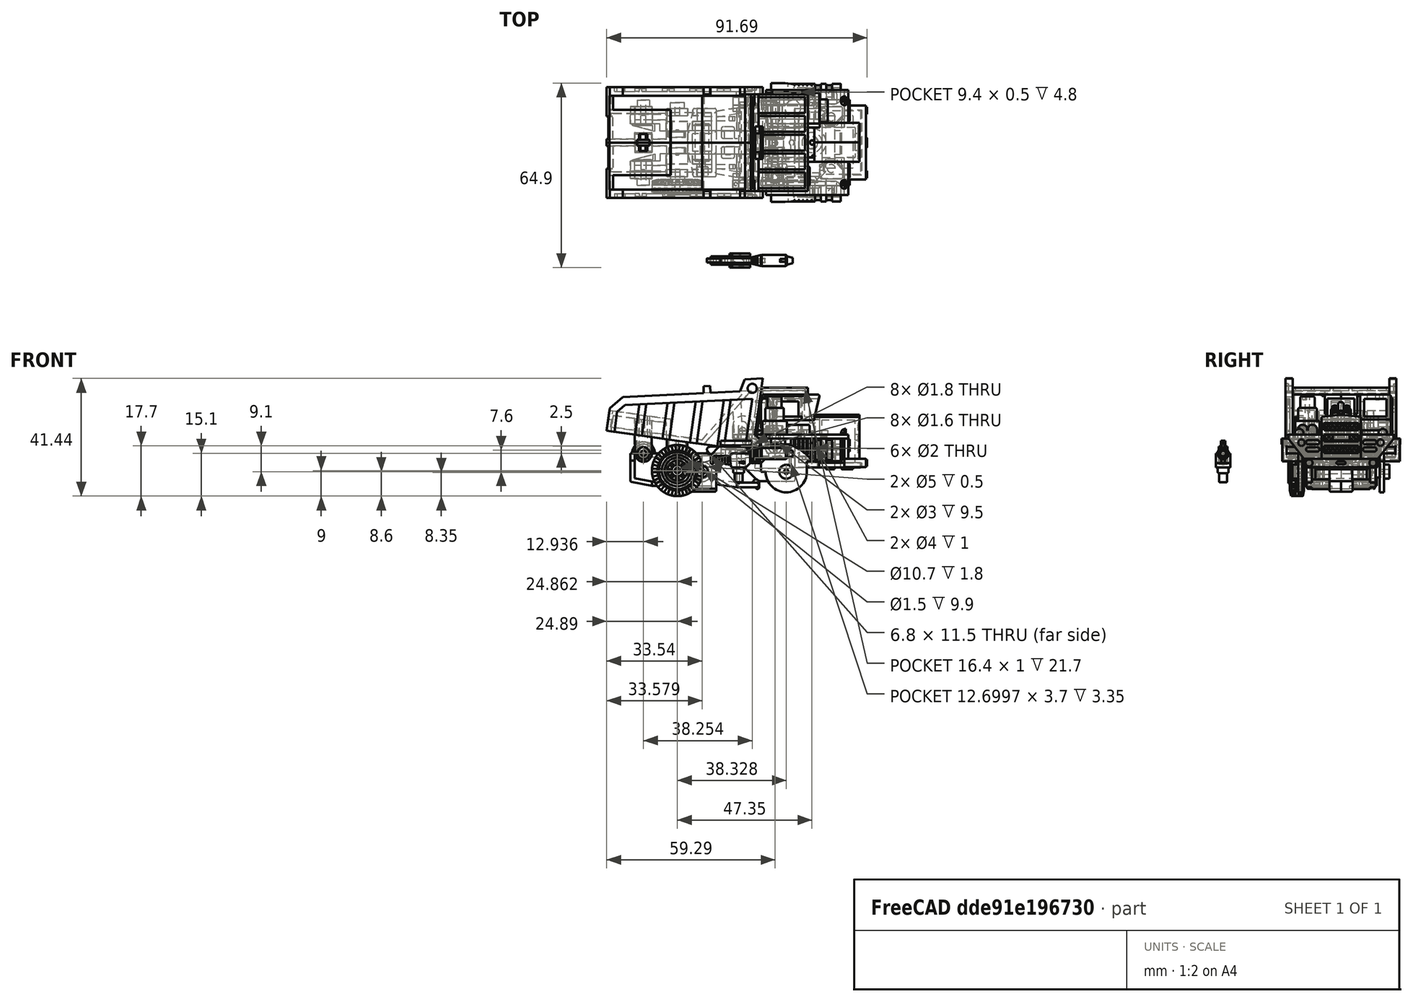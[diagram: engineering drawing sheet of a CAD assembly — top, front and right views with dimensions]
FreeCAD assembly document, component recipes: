
FREECAD ASSEMBLY — COMPONENT RECIPES ("Longhaul")

This assembly document has 21 components, labeled P0..P20 below (a component is one placed body or linked part). 19 of them carry a construction recipe — the FreeCAD feature program that regenerates the part from scratch, quoted from this document or its linked companion documents; the rest are supplied as boundary geometry only. No exploded tour is included for this assembly.
NOTE — document 2 of 4 of this assembly tour. The two overview renders and the header above are repeated from document 1; the component sections below continue where the previous document stopped.
COMPONENT P3 — recipe-attached ("Pre_Left_Leg", modeled in this document).
Construction recipe (the document's own serialized feature program — sketch geometry with constraints, then the solid features built on it; lengths are millimeters unless a unit is written):

FEATURE [PartDesign::SubShapeBinder] Binder002
  BindCopyOnChange = 0
  BindMode = 2
  ClaimChildren = false
  Context = -> Body003 [Binder002.]
  Fuse = false
  MakeFace = true
  OffsetFill = false
  OffsetIntersection = false
  OffsetJoinType = 0
  OffsetOpenResult = false
  PartialLoad = false
  Refine = true
  Relative = true
  _Version = 2
FEATURE [Sketcher::SketchObject] Sketch124
  ArcFitTolerance = 1e-06
  AttachmentSupport = -> [Binder002]
  ExternalGeometry = -> [Binder002]
  FullyConstrained = true
  MakeInternals = false
  MapMode = 5
  Placement = pos=(0,-7.1,0) rot=(1,0,0;1.5708rad)
  sketch-geometry (6):
    g0: ArcOfCircle CenterX=-23.6 CenterY=7.5 CenterZ=0 NormalX=0 NormalY=0 NormalZ=1 AngleXU=0 Radius=2.5 StartAngle=1.5708 EndAngle=4.71239
    g1: LineSegment StartX=-23.6 StartY=10 StartZ=0 EndX=-19.1 EndY=10 EndZ=0
    g2: LineSegment StartX=-19.1 StartY=10 StartZ=0 EndX=-19.1 EndY=2.1 EndZ=0
    g3: LineSegment StartX=-19.1 StartY=2.1 StartZ=0 EndX=-22.1 EndY=2.1 EndZ=0
    g4: LineSegment StartX=-22.1 StartY=2.1 StartZ=0 EndX=-22.1 EndY=5 EndZ=0
    g5: LineSegment StartX=-22.1 StartY=5 StartZ=0 EndX=-23.6 EndY=5 EndZ=0
  constraints (18):
    c: PointOnObject(g0,g-4)
    c: Coincident(g0,g-4)
    c: DistanceX(g0,g0) = 0
    c: DistanceX(g0,g0) = 0
    c: Coincident(g1,g0)
    c: Horizontal(g1)
    c: Coincident(g2,g1)
    c: Vertical(g2)
    c: Coincident(g3,g2)
    c: Horizontal(g3)
    c: Coincident(g4,g3)
    c: Vertical(g4)
    c: Coincident(g5,g4)
    c: Coincident(g5,g0)
    c: Horizontal(g5)
    c: DistanceX(g3,g3) = 3
    c: DistanceY(g2,g2) = 7.9
    c: DistanceX(g5,g5) = 1.5
FEATURE [PartDesign::Pad] Pad073
  Direction = (0,-1,2e-16)
  Length = 5.1
  Length2 = 10
  Profile = -> Sketch124
  ReferenceAxis = -> Sketch124 [N_Axis]
  Refine = true
  Suppressed = false
  Type = 0
FEATURE [Sketcher::SketchObject] Sketch125
  ArcFitTolerance = 1e-06
  AttachmentSupport = -> [Pad073]
  ExternalGeometry = -> [Pad073]
  FullyConstrained = true
  MakeInternals = false
  MapMode = 5
  Placement = pos=(0,-7.1,1.6e-15) rot=(0,0.707107,0.707107;3.14159rad)
  sketch-geometry (6):
    g0: LineSegment StartX=19.1 StartY=10 StartZ=0 EndX=19.1 EndY=2.1 EndZ=0
    g1: LineSegment StartX=19.1 StartY=2.1 StartZ=0 EndX=22.1 EndY=2.1 EndZ=0
    g2: LineSegment StartX=22.1 StartY=2.1 StartZ=0 EndX=22.1 EndY=5 EndZ=0
    g3: LineSegment StartX=22.1 StartY=5 StartZ=0 EndX=20.6 EndY=5 EndZ=0
    g4: LineSegment StartX=20.6 StartY=5 StartZ=0 EndX=20.6 EndY=10 EndZ=0
    g5: LineSegment StartX=20.6 StartY=10 StartZ=0 EndX=19.1 EndY=10 EndZ=0
  constraints (15):
    c: Coincident(g0,g-6)
    c: Coincident(g0,g-5)
    c: Coincident(g1,g0)
    c: Coincident(g1,g-4)
    c: PointOnObject(g2,g1)
    c: Coincident(g2,g-3)
    c: Vertical(g2)
    c: Coincident(g3,g2)
    c: Horizontal(g3)
    c: PointOnObject(g4,g-6)
    c: Coincident(g5,g4)
    c: Coincident(g5,g0)
    c: Coincident(g3,g4)
    c: DistanceX(g5,g5) = 1.5
    c: Vertical(g4)
FEATURE [PartDesign::Pad] Pad074
  BaseFeature = -> Pad073
  Direction = (0,1,-2e-16)
  Length = 3
  Length2 = 10
  Profile = -> Sketch125
  ReferenceAxis = -> Sketch125 [N_Axis]
  Refine = true
  Suppressed = false
  Type = 0
FEATURE [Sketcher::SketchObject] Sketch126
  ArcFitTolerance = 1e-06
  AttachmentSupport = -> [Pad074]
  ExternalGeometry = -> [Pad074]
  FullyConstrained = true
  MakeInternals = false
  MapMode = 5
  Placement = pos=(0,-12.2,2.8e-15) rot=(1,0,0;1.5708rad)
  sketch-geometry (1):
    g0: Circle CenterX=-23.6 CenterY=7.5 CenterZ=0 NormalX=0 NormalY=0 NormalZ=1 AngleXU=0 Radius=0.75
  constraints (2):
    c: Coincident(g0,g-3)
    c: Diameter(g0) = 1.5
FEATURE [PartDesign::Pocket] Pocket055
  BaseFeature = -> Pad074
  Direction = (0,1,-2e-16)
  Length = 6
  Length2 = 5
  Profile = -> Sketch126
  ReferenceAxis = -> Sketch126 [N_Axis]
  Refine = true
  Suppressed = false
  Type = 0
FEATURE [Sketcher::SketchObject] Sketch127
  ArcFitTolerance = 1e-06
  AttachmentSupport = -> [Pocket055]
  ExternalGeometry = -> [Pocket055]
  FullyConstrained = true
  MakeInternals = false
  MapMode = 5
  Placement = pos=(0,-12.2,2.8e-15) rot=(1,0,0;1.5708rad)
  sketch-geometry (8):
    g0: LineSegment StartX=-10.77 StartY=2.1 StartZ=0 EndX=-10.77 EndY=7.75 EndZ=0
    g1: ArcOfCircle CenterX=-10.77 CenterY=8.875 CenterZ=0 NormalX=0 NormalY=0 NormalZ=1 AngleXU=0 Radius=1.125 StartAngle=1.5708 EndAngle=4.71239
    g2: LineSegment StartX=-10.77 StartY=10 StartZ=0 EndX=-9.17 EndY=10 EndZ=0
    g3: ArcOfCircle CenterX=-9.17 CenterY=9.35 CenterZ=0 NormalX=0 NormalY=0 NormalZ=1 AngleXU=0 Radius=0.65 StartAngle=4.71239 EndAngle=7.85398
    g4: LineSegment StartX=-9.17 StartY=8.7 StartZ=0 EndX=-9.17 EndY=1.1 EndZ=0
    g5: LineSegment StartX=-9.17 StartY=1.1 StartZ=0 EndX=-21.1 EndY=1.1 EndZ=0
    g6: LineSegment StartX=-21.1 StartY=1.1 StartZ=0 EndX=-21.1 EndY=2.1 EndZ=0
    g7: LineSegment StartX=-21.1 StartY=2.1 StartZ=0 EndX=-10.77 EndY=2.1 EndZ=0
  constraints (27):
    c: Coincident(g1,g0)
    c: Coincident(g2,g1)
    c: Horizontal(g2)
    c: Coincident(g3,g2)
    c: Coincident(g4,g3)
    c: Vertical(g4)
    c: Coincident(g5,g4)
    c: Horizontal(g5)
    c: Coincident(g6,g5)
    c: DistanceY(g6,g6) = 1
    c: Vertical(g0)
    c: DistanceX(g-3,g0) = 8.33
    c: Diameter(g1) = 2.25
    c: DistanceX(g1,g0) = 0
    c: DistanceX(g1,g1) = 0
    c: DistanceX(g2,g2) = 1.6
    c: Diameter(g3) = 1.3
    c: DistanceX(g3,g2) = 0
    c: DistanceX(g3,g3) = 0
    c: DistanceY(g-4,g-4) = 7.9
    c: DistanceY(g0,g1) = 7.9
    c: Vertical(g6)
    c: DistanceX(g-3,g6) = 1
    c: Coincident(g7,g6)
    c: Coincident(g7,g0)
    c: Horizontal(g7)
    c: PointOnObject(g6,g-3)
FEATURE [PartDesign::Pad] Pad075
  BaseFeature = -> Pocket055
  Direction = (0,-1,2e-16)
  Length = 8.1
  Length2 = 10
  Profile = -> Sketch127
  ReferenceAxis = -> Sketch127 [N_Axis]
  Refine = true
  Reversed = true
  Suppressed = false
  Type = 0
FEATURE [Sketcher::SketchObject] Sketch128
  ArcFitTolerance = 1e-06
  AttachmentSupport = -> [Pad075]
  ExternalGeometry = -> [Pad075]
  FullyConstrained = true
  MakeInternals = false
  MapMode = 5
  Placement = pos=(0,5e-16,2.1) rot=(0,0,1;0rad)
  sketch-geometry (4):
    g0: LineSegment StartX=-19.1 StartY=-4.1 StartZ=0 EndX=-19.1 EndY=-10.2 EndZ=0
    g1: LineSegment StartX=-19.1 StartY=-10.2 StartZ=0 EndX=-10.77 EndY=-10.2 EndZ=0
    g2: LineSegment StartX=-10.77 StartY=-10.2 StartZ=0 EndX=-10.77 EndY=-4.1 EndZ=0
    g3: LineSegment StartX=-10.77 StartY=-4.1 StartZ=0 EndX=-19.1 EndY=-4.1 EndZ=0
  constraints (11):
    c: Coincident(g0,g1)
    c: Coincident(g1,g2)
    c: Coincident(g2,g3)
    c: Coincident(g3,g0)
    c: Vertical(g0)
    c: Vertical(g2)
    c: Horizontal(g1)
    c: Horizontal(g3)
    c: PointOnObject(g1,g-4)
    c: DistanceY(g-6,g1) = 2
    c: Coincident(g0,g-5)
FEATURE [PartDesign::Pocket] Pocket056
  BaseFeature = -> Pad075
  Direction = (0,0,-1)
  Length = 5
  Length2 = 5
  Profile = -> Sketch128
  ReferenceAxis = -> Sketch128 [N_Axis]
  Refine = true
  Suppressed = false
  Type = 0
FEATURE [Sketcher::SketchObject] Sketch129
  ArcFitTolerance = 1e-06
  AttachmentSupport = -> [Pocket056]
  ExternalGeometry = -> [Pocket056]
  FullyConstrained = true
  MakeInternals = false
  MapMode = 5
  Placement = pos=(0,-12.2,0) rot=(1,0,0;1.5708rad)
  sketch-geometry (4):
    g0: ArcOfCircle CenterX=-10.77 CenterY=8.875 CenterZ=0 NormalX=0 NormalY=0 NormalZ=1 AngleXU=0 Radius=1.125 StartAngle=1.5708 EndAngle=4.71239
    g1: ArcOfCircle CenterX=-9.17 CenterY=9.35 CenterZ=0 NormalX=0 NormalY=0 NormalZ=1 AngleXU=0 Radius=0.65 StartAngle=4.71239 EndAngle=7.85398
    g2: LineSegment StartX=-10.77 StartY=10 StartZ=0 EndX=-10.77 EndY=7.75 EndZ=0
    g3: LineSegment StartX=-9.17 StartY=10 StartZ=0 EndX=-9.17 EndY=8.7 EndZ=0
  constraints (8):
    c: Tangent(g0,g-4) = -1.5708
    c: Coincident(g0,g-4)
    c: Tangent(g1,g-3) = -1.5708
    c: Coincident(g1,g-3)
    c: Coincident(g2,g0)
    c: Coincident(g2,g0)
    c: Coincident(g3,g1)
    c: Coincident(g3,g1)
FEATURE [PartDesign::Pocket] Pocket057
  BaseFeature = -> Pocket056
  Direction = (0,1,-2e-16)
  Length = 2
  Length2 = 5
  Profile = -> Sketch129
  ReferenceAxis = -> Sketch129 [N_Axis]
  Refine = true
  Suppressed = false
  Type = 0
FEATURE [PartDesign::Fillet] Fillet004
  Base = -> Pocket057 [Edge38,Edge37]
  BaseFeature = -> Pocket057
  Radius = 0.5
  Refine = true
  SupportTransform = false
  Suppressed = false
  UseAllEdges = false
FEATURE [Sketcher::SketchObject] Sketch130
  ArcFitTolerance = 1e-06
  AttachmentSupport = -> [Fillet004]
  ExternalGeometry = -> [Fillet004]
  FullyConstrained = true
  MakeInternals = false
  MapMode = 5
  Placement = pos=(0,-12.2,0) rot=(1,0,0;1.5708rad)
  sketch-geometry (4):
    g0: LineSegment StartX=-10.77 StartY=2.1 StartZ=0 EndX=-10.77 EndY=3.1 EndZ=0
    g1: LineSegment StartX=-10.77 StartY=3.1 StartZ=0 EndX=-19.1 EndY=3.1 EndZ=0
    g2: LineSegment StartX=-19.1 StartY=3.1 StartZ=0 EndX=-19.1 EndY=2.1 EndZ=0
    g3: LineSegment StartX=-19.1 StartY=2.1 StartZ=0 EndX=-10.77 EndY=2.1 EndZ=0
  constraints (11):
    c: Coincident(g0,g1)
    c: Coincident(g1,g2)
    c: Coincident(g2,g3)
    c: Coincident(g3,g0)
    c: Vertical(g0)
    c: Vertical(g2)
    c: Horizontal(g1)
    c: Horizontal(g3)
    c: Coincident(g0,g-5)
    c: PointOnObject(g1,g-4)
    c: DistanceY(g2,g2) = 1
FEATURE [PartDesign::Pad] Pad076
  BaseFeature = -> Fillet004
  Direction = (0,-1,2e-16)
  Length = 2
  Length2 = 10
  Profile = -> Sketch130
  ReferenceAxis = -> Sketch130 [N_Axis]
  Refine = true
  Reversed = true
  Suppressed = false
  Type = 0
FEATURE [Sketcher::SketchObject] Sketch131
  ArcFitTolerance = 1e-06
  AttachmentSupport = -> [Pad076]
  ExternalGeometry = -> [Pad076]
  FullyConstrained = true
  MakeInternals = false
  MapMode = 5
  Placement = pos=(0,-12.2,0) rot=(1,0,0;1.5708rad)
  sketch-geometry (4):
    g0: LineSegment StartX=-21.1 StartY=2.1 StartZ=0 EndX=-21.1 EndY=1.1 EndZ=0
    g1: LineSegment StartX=-21.1 StartY=1.1 StartZ=0 EndX=-9.17 EndY=1.1 EndZ=0
    g2: LineSegment StartX=-9.17 StartY=1.1 StartZ=0 EndX=-9.17 EndY=2.1 EndZ=0
    g3: LineSegment StartX=-9.17 StartY=2.1 StartZ=0 EndX=-21.1 EndY=2.1 EndZ=0
  constraints (10):
    c: Coincident(g0,g1)
    c: Coincident(g1,g2)
    c: Coincident(g2,g3)
    c: Coincident(g3,g0)
    c: Vertical(g0)
    c: Vertical(g2)
    c: Horizontal(g1)
    c: Horizontal(g3)
    c: Coincident(g0,g-3)
    c: Coincident(g1,g-5)
FEATURE [PartDesign::Pocket] Pocket058
  BaseFeature = -> Pad076
  Direction = (0,1,-2e-16)
  Length = 9
  Length2 = 5
  Profile = -> Sketch131
  ReferenceAxis = -> Sketch131 [N_Axis]
  Refine = true
  Suppressed = false
  Type = 0
FEATURE [Sketcher::SketchObject] Sketch132
  ArcFitTolerance = 1e-06
  AttachmentOffset = pos=(0,0,-1) rot=(0,0,1;0rad)
  AttachmentSupport = -> [Pocket058]
  ExternalGeometry = -> [Pocket058]
  FullyConstrained = true
  MakeInternals = false
  MapMode = 5
  Placement = pos=(-21.1,0,0) rot=(0.57735,-0.57735,-0.57735;2.0944rad)
  sketch-geometry (16):
    g0: LineSegment StartX=12.2 StartY=2.1 StartZ=0 EndX=11 EndY=-5.15 EndZ=0
    g1: LineSegment StartX=4 StartY=-24.9 StartZ=0 EndX=6.5 EndY=-24.9 EndZ=0
    g2: LineSegment StartX=6.5 StartY=-24.9 StartZ=0 EndX=6.5 EndY=-35.4 EndZ=0
    g3: LineSegment StartX=6.5 StartY=-35.4 StartZ=0 EndX=10 EndY=-35.4 EndZ=0
    g4: LineSegment StartX=10 StartY=-35.4 StartZ=0 EndX=10 EndY=-22.8 EndZ=0
    g5: LineSegment StartX=10 StartY=-22.8 StartZ=0 EndX=9.5 EndY=-22.8 EndZ=0
    g6: LineSegment StartX=9.5 StartY=-22.8 StartZ=0 EndX=9.5 EndY=-11.9 EndZ=0
    g7: LineSegment StartX=9.5 StartY=-11.9 StartZ=0 EndX=12 EndY=-11.9 EndZ=0
    g8: LineSegment StartX=12 StartY=-11.9 StartZ=0 EndX=12 EndY=-5.15 EndZ=0
    g9: LineSegment StartX=12 StartY=-5.15 StartZ=0 EndX=11 EndY=-5.15 EndZ=0
    g10: LineSegment StartX=4.1 StartY=2.1 StartZ=0 EndX=4.1 EndY=-5.15 EndZ=0
    g11: LineSegment StartX=4.1 StartY=-5.15 StartZ=0 EndX=-1.8e-15 EndY=-5.15 EndZ=0
    g12: LineSegment StartX=-1.8e-15 StartY=-5.15 StartZ=0 EndX=-1.8e-15 EndY=-15.15 EndZ=0
    g13: LineSegment StartX=4 StartY=-24.9 StartZ=0 EndX=4 EndY=-15.15 EndZ=0
    g14: LineSegment StartX=4 StartY=-15.15 StartZ=0 EndX=-1.8e-15 EndY=-15.15 EndZ=0
    g15: LineSegment StartX=4.1 StartY=2.1 StartZ=0 EndX=12.2 EndY=2.1 EndZ=0
  constraints (47):
    c: Coincident(g0,g-3)
    c: Horizontal(g1)
    c: Coincident(g2,g1)
    c: Vertical(g2)
    c: Coincident(g3,g2)
    c: Horizontal(g3)
    c: Coincident(g4,g3)
    c: Vertical(g4)
    c: Coincident(g5,g4)
    c: Horizontal(g5)
    c: Coincident(g6,g5)
    c: Vertical(g6)
    c: Coincident(g7,g6)
    c: Horizontal(g7)
    c: Coincident(g8,g7)
    c: Vertical(g8)
    c: Coincident(g9,g8)
    c: Coincident(g9,g0)
    c: Horizontal(g9)
    c: DistanceX(g1,g6) = 5.5
    c: DistanceY(g8,g8) = 6.75
    c: DistanceY(g8,g0) = 7.25
    c: DistanceX(g9,g9) = 1
    c: Coincident(g10,g-3)
    c: Vertical(g10)
    c: Coincident(g11,g10)
    c: Horizontal(g11)
    c: Coincident(g12,g11)
    c: Vertical(g12)
    c: Coincident(g13,g1)
    c: Vertical(g13)
    c: Coincident(g14,g13)
    c: Coincident(g14,g12)
    c: Horizontal(g14)
    c: DistanceX(g11,g8) = 12
    c: DistanceX(g7,g7) = 2.5
    c: DistanceY(g10,g10) = 7.25
    c: DistanceY(g12,g12) = 10
    c: DistanceX(g11,g11) = 4.1
    c: DistanceX(g1,g1) = 2.5
    c: DistanceY(g3,g-4) = 45.4
    c: DistanceY(g1,g-5) = 34.9
    c: DistanceX(g5,g5) = 0.5
    c: DistanceX(g3,g3) = 3.5
    c: DistanceY(g4,g4) = 12.6
    c: Coincident(g15,g10)
    c: Coincident(g15,g0)
FEATURE [PartDesign::Pad] Pad077
  BaseFeature = -> Pocket058
  Direction = (-1,0,0)
  Length = 1
  Length2 = 10
  Profile = -> Sketch132
  ReferenceAxis = -> Sketch132 [N_Axis]
  Refine = true
  Reversed = true
  Suppressed = false
  Type = 0
FEATURE [Sketcher::SketchObject] Sketch133
  ArcFitTolerance = 1e-06
  AttachmentSupport = -> [Pad077]
  ExternalGeometry = -> [Pad077]
  FullyConstrained = true
  MakeInternals = false
  MapMode = 5
  Placement = pos=(-20.1,0,0) rot=(0.57735,0.57735,0.57735;2.0944rad)
  sketch-geometry (4):
    g0: LineSegment StartX=-4.1 StartY=2.1 StartZ=0 EndX=-12.2 EndY=2.1 EndZ=0
    g1: LineSegment StartX=-12.2 StartY=2.1 StartZ=0 EndX=-11 EndY=-5.15 EndZ=0
    g2: LineSegment StartX=-11 StartY=-5.15 StartZ=0 EndX=-4.1 EndY=-5.15 EndZ=0
    g3: LineSegment StartX=-4.1 StartY=-5.15 StartZ=0 EndX=-4.1 EndY=2.1 EndZ=0
  constraints (8):
    c: Coincident(g0,g-3)
    c: Coincident(g0,g-4)
    c: Coincident(g1,g0)
    c: Coincident(g1,g-4)
    c: Coincident(g2,g1)
    c: Coincident(g2,g-3)
    c: Coincident(g3,g2)
    c: Coincident(g3,g0)
FEATURE [PartDesign::Pad] Pad078
  BaseFeature = -> Pad077
  Direction = (1,0,0)
  Length = 1
  Length2 = 10
  Profile = -> Sketch133
  ReferenceAxis = -> Sketch133 [N_Axis]
  Refine = true
  Suppressed = false
  Type = 0
FEATURE [Sketcher::SketchObject] Sketch134
  ArcFitTolerance = 1e-06
  AttachmentSupport = -> [Pad078]
  ExternalGeometry = -> [Pad078]
  FullyConstrained = true
  MakeInternals = false
  MapMode = 5
  Placement = pos=(-20.1,0,0) rot=(0.57735,0.57735,0.57735;2.0944rad)
  sketch-geometry (8):
    g0: LineSegment StartX=-4 StartY=-15.15 StartZ=0 EndX=-4 EndY=-24.9 EndZ=0
    g1: LineSegment StartX=-4 StartY=-24.9 StartZ=0 EndX=-6.5 EndY=-24.9 EndZ=0
    g2: LineSegment StartX=-6.5 StartY=-24.9 StartZ=0 EndX=-6.5 EndY=-35.4 EndZ=0
    g3: LineSegment StartX=-6.5 StartY=-35.4 StartZ=0 EndX=-10 EndY=-35.4 EndZ=0
    g4: LineSegment StartX=-10 StartY=-35.4 StartZ=0 EndX=-10 EndY=-22.8 EndZ=0
    g5: LineSegment StartX=-4 StartY=-15.15 StartZ=0 EndX=-9.5 EndY=-15.15 EndZ=0
    g6: LineSegment StartX=-9.5 StartY=-15.15 StartZ=0 EndX=-9.5 EndY=-22.8 EndZ=0
    g7: LineSegment StartX=-9.5 StartY=-22.8 StartZ=0 EndX=-10 EndY=-22.8 EndZ=0
  constraints (17):
    c: Coincident(g0,g-3)
    c: Coincident(g0,g-9)
    c: Coincident(g1,g0)
    c: Coincident(g1,g-9)
    c: Coincident(g2,g1)
    c: Coincident(g2,g-6)
    c: Coincident(g3,g2)
    c: Coincident(g3,g-7)
    c: Coincident(g4,g3)
    c: Coincident(g4,g-8)
    c: Coincident(g5,g0)
    c: PointOnObject(g5,g-4)
    c: Horizontal(g5)
    c: Coincident(g6,g5)
    c: Coincident(g6,g-8)
    c: Coincident(g7,g4)
    c: Coincident(g6,g7)
FEATURE [PartDesign::Pad] Pad079
  BaseFeature = -> Pad078
  Direction = (1,0,0)
  Length = 0.5
  Length2 = 10
  Profile = -> Sketch134
  ReferenceAxis = -> Sketch134 [N_Axis]
  Refine = true
  Suppressed = false
  Type = 0
FEATURE [Sketcher::SketchObject] Sketch135
  ArcFitTolerance = 1e-06
  AttachmentSupport = -> [Pad079]
  ExternalGeometry = -> [Pad079]
  FullyConstrained = true
  MakeInternals = false
  MapMode = 5
  Placement = pos=(0,1.8e-15,0) rot=(0,0.707107,0.707107;3.14159rad)
  sketch-geometry (8):
    g0: LineSegment StartX=20.1 StartY=-5.15 StartZ=0 EndX=7.6 EndY=-5.15 EndZ=0
    g1: LineSegment StartX=20.1 StartY=-15.15 StartZ=0 EndX=7.6 EndY=-15.15 EndZ=0
    g2: LineSegment StartX=7.6 StartY=-5.15 StartZ=0 EndX=7.6 EndY=-15.15 EndZ=0
    g3: LineSegment StartX=20.1 StartY=-15.15 StartZ=0 EndX=20.1 EndY=-13.55 EndZ=0
    g4: LineSegment StartX=20.1 StartY=-13.55 StartZ=0 EndX=8.6 EndY=-13.55 EndZ=0
    g5: LineSegment StartX=8.6 StartY=-13.55 StartZ=0 EndX=8.6 EndY=-6.75 EndZ=0
    g6: LineSegment StartX=8.6 StartY=-6.75 StartZ=0 EndX=20.1 EndY=-6.75 EndZ=0
    g7: LineSegment StartX=20.1 StartY=-6.75 StartZ=0 EndX=20.1 EndY=-5.15 EndZ=0
  constraints (23):
    c: Coincident(g0,g-5)
    c: Horizontal(g0)
    c: Coincident(g1,g-4)
    c: Horizontal(g1)
    c: Coincident(g2,g0)
    c: Coincident(g2,g1)
    c: Vertical(g2)
    c: DistanceY(g-6,g-6) = 10
    c: Coincident(g3,g1)
    c: Vertical(g3)
    c: Coincident(g4,g3)
    c: Horizontal(g4)
    c: Coincident(g5,g4)
    c: Vertical(g5)
    c: Coincident(g6,g5)
    c: Horizontal(g6)
    c: PointOnObject(g6,g-7)
    c: Coincident(g7,g6)
    c: Coincident(g7,g0)
    c: DistanceX(g0,g5) = 1
    c: DistanceY(g5,g0) = 1.6
    c: DistanceY(g1,g4) = 1.6
    c: DistanceX(g0,g6) = 12.5
FEATURE [PartDesign::Pad] Pad080
  BaseFeature = -> Pad079
  Direction = (0,1,-2e-16)
  Length = 4.1
  Length2 = 10
  Profile = -> Sketch135
  ReferenceAxis = -> Sketch135 [N_Axis]
  Refine = true
  Reversed = true
  Suppressed = false
  Type = 0
FEATURE [Sketcher::SketchObject] Sketch136
  ArcFitTolerance = 1e-06
  AttachmentSupport = -> [Pad080]
  ExternalGeometry = -> [Pad080]
  FullyConstrained = true
  MakeInternals = false
  MapMode = 5
  Placement = pos=(0,-12,0) rot=(1,0,0;1.5708rad)
  sketch-geometry (6):
    g0: LineSegment StartX=-20.1 StartY=-5.15 StartZ=0 EndX=-8.6 EndY=-5.15 EndZ=0
    g1: LineSegment StartX=-8.6 StartY=-5.15 StartZ=0 EndX=-8.6 EndY=-13.35 EndZ=0
    g2: LineSegment StartX=-20.1 StartY=-11.9 StartZ=0 EndX=-17.3 EndY=-11.9 EndZ=0
    g3: LineSegment StartX=-8.6 StartY=-13.35 StartZ=0 EndX=-14.6 EndY=-13.35 EndZ=0
    g4: ArcOfCircle CenterX=-14.6 CenterY=-10.1112 CenterZ=0 NormalX=0 NormalY=0 NormalZ=1 AngleXU=0 Radius=3.23879 StartAngle=3.72672 EndAngle=4.71239
    g5: LineSegment StartX=-20.1 StartY=-5.15 StartZ=0 EndX=-20.1 EndY=-11.9 EndZ=0
  constraints (20):
    c: DistanceX(g-4,g-4) = 1
    c: Coincident(g0,g-4)
    c: Horizontal(g0)
    c: DistanceX(g0,g0) = 11.5
    c: Coincident(g1,g0)
    c: Vertical(g1)
    c: DistanceY(g1,g1) = 8.2
    c: Coincident(g2,g-3)
    c: Horizontal(g2)
    c: Coincident(g3,g1)
    c: Horizontal(g3)
    c: Coincident(g4,g3)
    c: Coincident(g4,g2)
    c: DistanceX(g2,g2) = 2.8
    c: DistanceX(g4,g3) = 0
    c: DistanceX(g-5,g4) = 6.5
    c: DistanceX(g3,g1) = 6
    c: DistanceX(g2,g1) = 8.7
    c: Coincident(g5,g2)
    c: Coincident(g5,g0)
FEATURE [PartDesign::Pad] Pad081
  BaseFeature = -> Pad080
  Direction = (0,-1,2e-16)
  Length = 1.5
  Length2 = 10
  Profile = -> Sketch136
  ReferenceAxis = -> Sketch136 [N_Axis]
  Refine = true
  Reversed = true
  Suppressed = false
  Type = 0
FEATURE [Sketcher::SketchObject] Sketch137
  ArcFitTolerance = 1e-06
  AttachmentSupport = -> [Pad081]
  ExternalGeometry = -> [Pad081]
  FullyConstrained = true
  MakeInternals = false
  MapMode = 5
  Placement = pos=(-19.1,0,4.6e-15) rot=(0.57735,0.57735,0.57735;2.0944rad)
  sketch-geometry (4):
    g0: LineSegment StartX=-12.2 StartY=2.1 StartZ=0 EndX=-10.2 EndY=2.1 EndZ=0
    g1: LineSegment StartX=-12.2 StartY=2.1 StartZ=0 EndX=-11 EndY=-5.15 EndZ=0
    g2: LineSegment StartX=-11 StartY=-5.15 StartZ=0 EndX=-9 EndY=-5.15 EndZ=0
    g3: LineSegment StartX=-9 StartY=-5.15 StartZ=0 EndX=-10.2 EndY=2.1 EndZ=0
  constraints (10):
    c: DistanceX(g-4,g-4) = 2
    c: Coincident(g0,g-4)
    c: Coincident(g0,g-4)
    c: Coincident(g1,g0)
    c: Coincident(g1,g-5)
    c: Coincident(g2,g1)
    c: PointOnObject(g2,g-6)
    c: Coincident(g3,g2)
    c: Coincident(g3,g0)
    c: DistanceX(g2,g2) = 2
FEATURE [PartDesign::Pad] Pad082
  BaseFeature = -> Pad081
  Direction = (1,0,0)
  Length = 9.93
  Length2 = 10
  Profile = -> Sketch137
  ReferenceAxis = -> Sketch137 [N_Axis]
  Refine = true
  Suppressed = false
  Type = 0
FEATURE [Sketcher::SketchObject] Sketch138
  ArcFitTolerance = 1e-06
  AttachmentSupport = -> [Pad082]
  ExternalGeometry = -> [Pad082]
  FullyConstrained = true
  MakeInternals = false
  MapMode = 5
  Placement = pos=(0,-12.2,0) rot=(1,0,0;1.5708rad)
  sketch-geometry (3):
    g0: LineSegment StartX=-9.17 StartY=2.1 StartZ=0 EndX=-9.17 EndY=-5.15 EndZ=0
    g1: LineSegment StartX=-9.17 StartY=-5.15 StartZ=0 EndX=-10.1 EndY=-5.15 EndZ=0
    g2: LineSegment StartX=-10.1 StartY=-5.15 StartZ=0 EndX=-9.17 EndY=2.1 EndZ=0
  constraints (7):
    c: Coincident(g0,g-3)
    c: Coincident(g0,g-3)
    c: Coincident(g1,g0)
    c: PointOnObject(g1,g-4)
    c: Coincident(g2,g1)
    c: Coincident(g2,g0)
    c: DistanceX(g-4,g1) = 11
FEATURE [PartDesign::Pocket] Pocket059
  BaseFeature = -> Pad082
  Direction = (0,1,-2e-16)
  Length = 5
  Length2 = 5
  Profile = -> Sketch138
  ReferenceAxis = -> Sketch138 [N_Axis]
  Refine = true
  Suppressed = false
  Type = 0
FEATURE [Sketcher::SketchObject] Sketch139
  ArcFitTolerance = 1e-06
  AttachmentSupport = -> [Pocket059]
  ExternalGeometry = -> [Pocket059]
  FullyConstrained = true
  MakeInternals = false
  MapMode = 5
  Placement = pos=(0,-4.1,0) rot=(0,0.707107,0.707107;3.14159rad)
  sketch-geometry (4):
    g0: LineSegment StartX=9.17 StartY=2.1 StartZ=0 EndX=10.77 EndY=2.1 EndZ=0
    g1: LineSegment StartX=9.17 StartY=2.1 StartZ=0 EndX=10.1 EndY=-5.15 EndZ=0
    g2: LineSegment StartX=10.1 StartY=-5.15 StartZ=0 EndX=11.7 EndY=-5.15 EndZ=0
    g3: LineSegment StartX=11.7 StartY=-5.15 StartZ=0 EndX=10.77 EndY=2.1 EndZ=0
  constraints (9):
    c: Coincident(g0,g-4)
    c: Coincident(g0,g-3)
    c: Coincident(g1,g0)
    c: Coincident(g1,g-4)
    c: Coincident(g2,g1)
    c: PointOnObject(g2,g-5)
    c: Coincident(g3,g2)
    c: Coincident(g3,g0)
    c: DistanceX(g2,g2) = 1.6
FEATURE [PartDesign::Pad] Pad083
  BaseFeature = -> Pocket059
  Direction = (0,1,-2e-16)
  Length = 6.5
  Length2 = 10
  Profile = -> Sketch139
  ReferenceAxis = -> Sketch139 [N_Axis]
  Refine = true
  Reversed = true
  Suppressed = false
  Type = 0
FEATURE [Sketcher::SketchObject] Sketch140
  ArcFitTolerance = 1e-06
  AttachmentSupport = -> [Pad083]
  ExternalGeometry = -> [Pad083]
  FullyConstrained = true
  MakeInternals = false
  MapMode = 5
  Placement = pos=(-8.6,0,0) rot=(0.57735,0.57735,0.57735;2.0944rad)
  sketch-geometry (4):
    g0: LineSegment StartX=-10.5 StartY=-5.15 StartZ=0 EndX=-4.1 EndY=-5.15 EndZ=0
    g1: LineSegment StartX=-4.1 StartY=-5.15 StartZ=0 EndX=-4.1 EndY=-15.15 EndZ=0
    g2: LineSegment StartX=-4.1 StartY=-15.15 StartZ=0 EndX=-10.5 EndY=-13.35 EndZ=0
    g3: LineSegment StartX=-10.5 StartY=-13.35 StartZ=0 EndX=-10.5 EndY=-5.15 EndZ=0
  constraints (8):
    c: Coincident(g0,g-3)
    c: Coincident(g0,g-4)
    c: Coincident(g1,g0)
    c: Coincident(g1,g-4)
    c: Coincident(g2,g1)
    c: Coincident(g2,g-3)
    c: Coincident(g3,g2)
    c: Coincident(g3,g0)
FEATURE [PartDesign::Pad] Pad084
  BaseFeature = -> Pad083
  Direction = (1,0,0)
  Length = 1
  Length2 = 10
  Profile = -> Sketch140
  ReferenceAxis = -> Sketch140 [N_Axis]
  Refine = true
  Reversed = true
  Suppressed = false
  Type = 0
FEATURE [Sketcher::SketchObject] Sketch141
  ArcFitTolerance = 1e-06
  AttachmentSupport = -> [Pad084]
  ExternalGeometry = -> [Pad084]
  FullyConstrained = false
  MakeInternals = false
  MapMode = 5
  Placement = pos=(0,-4.1,0) rot=(0,0.707107,0.707107;3.14159rad)
  sketch-geometry (4):
    g0: LineSegment StartX=8.6 StartY=-6.7914 StartZ=0 EndX=8.6 EndY=-13.55 EndZ=0
    g1: LineSegment StartX=8.6 StartY=-13.55 StartZ=0 EndX=9.6 EndY=-13.55 EndZ=0
    g2: LineSegment StartX=9.6 StartY=-13.55 StartZ=0 EndX=9.6 EndY=-6.7914 EndZ=0
    g3: LineSegment StartX=9.6 StartY=-6.7914 StartZ=0 EndX=8.6 EndY=-6.7914 EndZ=0
  constraints (10):
    c: Coincident(g0,g1)
    c: Coincident(g1,g2)
    c: Coincident(g2,g3)
    c: Coincident(g3,g0)
    c: Vertical(g0)
    c: Vertical(g2)
    c: Horizontal(g1)
    c: Horizontal(g3)
    c: PointOnObject(g0,g-3)
    c: Coincident(g1,g-4)
FEATURE [PartDesign::Pad] Pad085
  BaseFeature = -> Pad084
  Direction = (0,1,-2e-16)
  Length = 1
  Length2 = 10
  Profile = -> Sketch141
  ReferenceAxis = -> Sketch141 [N_Axis]
  Refine = true
  Suppressed = false
  Type = 0
FEATURE [Sketcher::SketchObject] Sketch142
  ArcFitTolerance = 1e-06
  AttachmentSupport = -> [Pad085]
  ExternalGeometry = -> [Pad085]
  FullyConstrained = true
  MakeInternals = false
  MapMode = 5
  Placement = pos=(0,-4.1,0) rot=(1,0,0;1.5708rad)
  sketch-geometry (4):
    g0: LineSegment StartX=-9.6 StartY=-5.15 StartZ=0 EndX=-20.1 EndY=-5.15 EndZ=0
    g1: LineSegment StartX=-20.1 StartY=-5.15 StartZ=0 EndX=-20.1 EndY=-6.75 EndZ=0
    g2: LineSegment StartX=-20.1 StartY=-6.75 StartZ=0 EndX=-9.6 EndY=-6.75 EndZ=0
    g3: LineSegment StartX=-9.6 StartY=-6.75 StartZ=0 EndX=-9.6 EndY=-5.15 EndZ=0
  constraints (10):
    c: Coincident(g0,g1)
    c: Coincident(g1,g2)
    c: Coincident(g2,g3)
    c: Coincident(g3,g0)
    c: Horizontal(g0)
    c: Horizontal(g2)
    c: Vertical(g1)
    c: Vertical(g3)
    c: Coincident(g0,g-6)
    c: Coincident(g1,g-5)
FEATURE [PartDesign::Pad] Pad086
  BaseFeature = -> Pad085
  Direction = (0,-1,2e-16)
  Length = 7
  Length2 = 10
  Profile = -> Sketch142
  ReferenceAxis = -> Sketch142 [N_Axis]
  Refine = true
  Suppressed = false
  Type = 0
FEATURE [Sketcher::SketchObject] Sketch143
  ArcFitTolerance = 1e-06
  AttachmentSupport = -> [Pad086]
  ExternalGeometry = -> [Pad086]
  FullyConstrained = true
  MakeInternals = false
  MapMode = 5
  Placement = pos=(0,-10.5,0) rot=(0,0.707107,0.707107;3.14159rad)
  sketch-geometry (8):
    g0: LineSegment StartX=9.6 StartY=-13.35 StartZ=0 EndX=14.6 EndY=-13.35 EndZ=0
    g1: ArcOfCircle CenterX=14.6 CenterY=-10.1112 CenterZ=0 NormalX=0 NormalY=0 NormalZ=1 AngleXU=0 Radius=3.23879 StartAngle=4.71239 EndAngle=5.69806
    g2: LineSegment StartX=17.3 StartY=-11.9 StartZ=0 EndX=20.1 EndY=-11.9 EndZ=0
    g3: LineSegment StartX=20.1 StartY=-11.9 StartZ=0 EndX=20.1 EndY=-10.4 EndZ=0
    g4: LineSegment StartX=20.1 StartY=-10.4 StartZ=0 EndX=16.3146 EndY=-10.4 EndZ=0
    g5: LineSegment StartX=9.6 StartY=-13.35 StartZ=0 EndX=9.6 EndY=-11.85 EndZ=0
    g6: LineSegment StartX=9.6 StartY=-11.85 StartZ=0 EndX=14.6 EndY=-11.85 EndZ=0
    g7: ArcOfCircle CenterX=14.6 CenterY=-10.1112 CenterZ=0 NormalX=0 NormalY=0 NormalZ=1 AngleXU=0 Radius=1.73879 StartAngle=4.71239 EndAngle=6.11632
  constraints (22):
    c: Coincident(g0,g-7)
    c: Coincident(g1,g0)
    c: Tangent(g1,g-5) = -1.5708
    c: PointOnObject(g2,g-5)
    c: Coincident(g2,g-4)
    c: Horizontal(g2)
    c: PointOnObject(g3,g2)
    c: PointOnObject(g3,g-3)
    c: Vertical(g3)
    c: Coincident(g4,g3)
    c: Horizontal(g4)
    c: Coincident(g0,g-6)
    c: Coincident(g5,g0)
    c: PointOnObject(g5,g-7)
    c: Coincident(g6,g5)
    c: Horizontal(g6)
    c: Coincident(g7,g6)
    c: Coincident(g7,g4)
    c: Coincident(g7,g1)
    c: DistanceY(g3,g3) = 1.5
    c: DistanceY(g5,g5) = 1.5
    c: DistanceX(g6,g0) = 0
FEATURE [PartDesign::Pad] Pad087
  BaseFeature = -> Pad086
  Direction = (0,1,-2e-16)
  Length = 1
  Length2 = 10
  Profile = -> Sketch143
  ReferenceAxis = -> Sketch143 [N_Axis]
  Refine = true
  Suppressed = false
  Type = 0
FEATURE [Sketcher::SketchObject] Sketch144
  ArcFitTolerance = 1e-06
  AttachmentSupport = -> [Pad087]
  ExternalGeometry = -> [Pad087]
  FullyConstrained = true
  MakeInternals = false
  MapMode = 5
  Placement = pos=(-9.9e-15,-9.5,0) rot=(1,0,0;1.5708rad)
  sketch-geometry (8):
    g0: LineSegment StartX=-19.6 StartY=-22.8 StartZ=0 EndX=-19.6 EndY=-15.15 EndZ=0
    g1: LineSegment StartX=-19.6 StartY=-15.15 StartZ=0 EndX=-20.1 EndY=-15.15 EndZ=0
    g2: LineSegment StartX=-20.1 StartY=-15.15 StartZ=0 EndX=-20.1 EndY=-10.4 EndZ=0
    g3: LineSegment StartX=-20.1 StartY=-10.4 StartZ=0 EndX=-16.3146 EndY=-10.4 EndZ=0
    g4: ArcOfCircle CenterX=-14.6 CenterY=-10.1112 CenterZ=0 NormalX=0 NormalY=0 NormalZ=1 AngleXU=0 Radius=1.73879 StartAngle=3.30845 EndAngle=4.71239
    g5: LineSegment StartX=-14.6 StartY=-11.85 StartZ=0 EndX=-9.6 EndY=-11.85 EndZ=0
    g6: LineSegment StartX=-19.6 StartY=-22.8 StartZ=0 EndX=-9.6 EndY=-22.8 EndZ=0
    g7: LineSegment StartX=-9.6 StartY=-11.85 StartZ=0 EndX=-9.6 EndY=-22.8 EndZ=0
  constraints (17):
    c: Coincident(g0,g-4)
    c: Coincident(g0,g-4)
    c: Coincident(g1,g0)
    c: Coincident(g1,g-3)
    c: Coincident(g2,g1)
    c: Coincident(g2,g-5)
    c: Coincident(g3,g2)
    c: Coincident(g3,g-7)
    c: Tangent(g4,g-7) = -1.5708
    c: Coincident(g4,g-8)
    c: Coincident(g5,g4)
    c: Coincident(g5,g-8)
    c: Coincident(g6,g0)
    c: Horizontal(g6)
    c: Coincident(g7,g5)
    c: Coincident(g6,g7)
    c: Vertical(g7)
FEATURE [PartDesign::Pad] Pad088
  BaseFeature = -> Pad087
  Direction = (-1e-15,-1,2e-16)
  Length = 2
  Length2 = 10
  Profile = -> Sketch144
  ReferenceAxis = -> Sketch144 [N_Axis]
  Refine = true
  Reversed = true
  Suppressed = false
  Type = 0
FEATURE [PartDesign::Body] Body003  label="Pre_Left_Leg"
  AllowCompound = false
  Group = -> [Binder002,Sketch124,Pad073,Sketch125,Pad074,Sketch126,Pocket055,Sketch127,Pad075,Sketch128,Pocket056,Sketch129,Pocket057,Fillet004,Sketch130,Pad076,Sketch131,Pocket058,Sketch132,Pad077,Sketch133,Pad078,Sketch134,Pad079,Sketch135,Pad080,Sketch136,Pad081,Sketch137,Pad082,Sketch138,Pocket059,Sketch139,Pad083,Sketch140,Pad084,Sketch141,Pad085,Sketch142,Pad086,Sketch143,Pad087,Sketch144,Pad088,+61 more]
  Origin = -> Origin003
  Placement = pos=(0,38,0) rot=(0,0,1;0rad)
  Tip = -> Pocket183
COMPONENT P4 — recipe-attached ("Right_Foot", modeled in this document).
Construction recipe (the document's own serialized feature program — sketch geometry with constraints, then the solid features built on it; lengths are millimeters unless a unit is written):

FEATURE [Sketcher::SketchObject] Sketch172
  ArcFitTolerance = 1e-06
  AttachmentSupport = -> [XY_Plane004]
  FullyConstrained = true
  MakeInternals = false
  MapMode = 5
  sketch-geometry (14):
    g0: LineSegment StartX=0 StartY=0 StartZ=0 EndX=43 EndY=0 EndZ=0
    g1: ArcOfCircle CenterX=50.8475 CenterY=2.65774 CenterZ=0 NormalX=0 NormalY=0 NormalZ=1 AngleXU=0 Radius=3.3 StartAngle=6.11336 EndAngle=7.54355
    g2: LineSegment StartX=51.8555 StartY=5.8 StartZ=0 EndX=51.8555 EndY=25.9 EndZ=0
    g3: LineSegment StartX=51.8555 StartY=25.9 StartZ=0 EndX=45.5709 EndY=24.6903 EndZ=0
    g4: LineSegment StartX=45.5709 StartY=24.6903 StartZ=0 EndX=44.5555 EndY=20.3063 EndZ=0
    g5: LineSegment StartX=44.5555 StartY=20.3063 StartZ=0 EndX=34.343 EndY=18.3406 EndZ=0
    g6: LineSegment StartX=34.343 StartY=18.3406 StartZ=0 EndX=33.8894 EndY=20.6973 EndZ=0
    g7: LineSegment StartX=33.8894 StartY=20.6973 StartZ=0 EndX=31.5326 EndY=20.2437 EndZ=0
    g8: LineSegment StartX=31.5326 StartY=20.2437 StartZ=0 EndX=31.9863 EndY=17.8869 EndZ=0
    g9: LineSegment StartX=31.9863 StartY=17.8869 StartZ=0 EndX=4 EndY=12.5 EndZ=0
    g10: LineSegment StartX=4 StartY=12.5 StartZ=0 EndX=0 EndY=8 EndZ=0
    g11: LineSegment StartX=0 StartY=8 StartZ=0 EndX=0 EndY=0 EndZ=0
    g12: ArcOfCircle CenterX=43 CenterY=15.82 CenterZ=0 NormalX=0 NormalY=0 NormalZ=1 AngleXU=0 Radius=15.82 StartAngle=4.71239 EndAngle=4.90962
    g13: LineSegment StartX=46.1 StartY=0.306702 StartZ=0 EndX=54.1 EndY=2.1 EndZ=0
  constraints (44):
    c: Coincident(g0,g-1)
    c: Coincident(g2,g1)
    c: Vertical(g2)
    c: Coincident(g3,g2)
    c: Coincident(g4,g3)
    c: Coincident(g5,g4)
    c: Coincident(g6,g5)
    c: Coincident(g7,g6)
    c: Coincident(g8,g7)
    c: Coincident(g10,g9)
    c: PointOnObject(g10,g-2)
    c: Coincident(g11,g10)
    c: Coincident(g11,g0)
    c: Parallel(g7,g5)
    c: Parallel(g3,g5)
    c: Parallel(g7,g9)
    c: Distance(g7) = 2.4
    c: Distance(g5) = 10.4
    c: Angle(g5,g6) = 1.5708
    c: Angle(g8,g9) = 1.5708
    c: Distance(g3) = 6.4
    c: DistanceY(g11,g11) = 8
    c: Distance(g8) = 2.4
    c: Distance(g6) = 2.4
    c: Coincident(g9,g8)
    c: Distance(g4) = 4.5
    c: DistanceX(g4,g2) = 7.3
    c: DistanceX(g0,g9) = 4
    c: DistanceY(g0,g9) = 12.5
    c: Distance(g9) = 28.5
    c: DistanceY(g0,g2) = 25.9
    c: DistanceX(g0,g1) = 54.1
    c: DistanceX(g0,g1) = 51.8555
    c: DistanceY(g1,g2) = 20.1
    c: PointOnObject(g0,g-1)
    c: Coincident(g12,g0)
    c: Coincident(g13,g12)
    c: Coincident(g13,g1)
    c: Tangent(g12,g-1)
    c: DistanceY(g1,g1) = 3.7
    c: Radius(g1) = 3.3
    c: DistanceX(g0,g0) = 43
    c: DistanceX(g12,g1) = 8
    c: Radius(g12) = 15.82
FEATURE [PartDesign::Pad] Pad102
  Direction = (0,0,1)
  Length = 1.5
  Length2 = 10
  Profile = -> Sketch172
  ReferenceAxis = -> Sketch172 [N_Axis]
  Refine = true
  Suppressed = false
  Type = 0
FEATURE [Sketcher::SketchObject] Sketch173
  ArcFitTolerance = 1e-06
  AttachmentSupport = -> [Pad102]
  ExternalGeometry = -> [Pad102]
  FullyConstrained = true
  MakeInternals = false
  MapMode = 5
  Placement = pos=(0,0,1.5) rot=(0,0,1;0rad)
  sketch-geometry (17):
    g0: LineSegment StartX=0 StartY=0 StartZ=0 EndX=0 EndY=8 EndZ=0
    g1: LineSegment StartX=0 StartY=8 StartZ=0 EndX=4 EndY=12.5 EndZ=0
    g2: LineSegment StartX=4 StartY=12.5 StartZ=0 EndX=31.9863 EndY=17.8869 EndZ=0
    g3: LineSegment StartX=31.9863 StartY=17.8869 StartZ=0 EndX=31.5326 EndY=20.2437 EndZ=0
    g4: LineSegment StartX=31.5326 StartY=20.2437 StartZ=0 EndX=33.8894 EndY=20.6973 EndZ=0
    g5: LineSegment StartX=33.8894 StartY=20.6973 StartZ=0 EndX=34.343 EndY=18.3406 EndZ=0
    g6: LineSegment StartX=34.343 StartY=18.3406 StartZ=0 EndX=44.5555 EndY=20.3063 EndZ=0
    g7: LineSegment StartX=44.5555 StartY=20.3063 StartZ=0 EndX=45.5709 EndY=24.6903 EndZ=0
    g8: LineSegment StartX=45.5709 StartY=24.6903 StartZ=0 EndX=51.8555 EndY=25.9 EndZ=0
    g9: LineSegment StartX=51.8555 StartY=25.9 StartZ=0 EndX=51.8555 EndY=5.8 EndZ=0
    g10: ArcOfCircle CenterX=50.8475 CenterY=2.65774 CenterZ=0 NormalX=0 NormalY=0 NormalZ=1 AngleXU=0 Radius=3.3 StartAngle=6.11336 EndAngle=7.54355
    g11: LineSegment StartX=54.1 StartY=2.1 StartZ=0 EndX=49.1555 EndY=0.991637 EndZ=0
    g12: LineSegment StartX=0 StartY=0 StartZ=0 EndX=2.7 EndY=0 EndZ=0
    g13: LineSegment StartX=2.7 StartY=0 StartZ=0 EndX=2.7 EndY=7.1 EndZ=0
    g14: LineSegment StartX=2.7 StartY=7.1 StartZ=0 EndX=5.1 EndY=9.8 EndZ=0
    g15: LineSegment StartX=5.1 StartY=9.8 StartZ=0 EndX=49.1555 EndY=18.28 EndZ=0
    g16: LineSegment StartX=49.1555 StartY=18.28 StartZ=0 EndX=49.1555 EndY=0.991637 EndZ=0
  constraints (40):
    c: Coincident(g0,g-1)
    c: Coincident(g0,g-12)
    c: Coincident(g1,g0)
    c: Coincident(g1,g-11)
    c: Coincident(g2,g1)
    c: Coincident(g2,g-10)
    c: Coincident(g3,g2)
    c: Coincident(g3,g-9)
    c: Coincident(g4,g3)
    c: Coincident(g4,g-8)
    c: Coincident(g5,g4)
    c: Coincident(g5,g-7)
    c: Coincident(g6,g5)
    c: Coincident(g6,g-6)
    c: Coincident(g7,g6)
    c: Coincident(g7,g-5)
    c: Coincident(g8,g7)
    c: Coincident(g8,g-4)
    c: Coincident(g9,g8)
    c: Coincident(g9,g-13)
    c: Coincident(g10,g9)
    c: Coincident(g10,g-14)
    c: Tangent(g10,g-13)
    c: Coincident(g11,g10)
    c: PointOnObject(g11,g-14)
    c: Coincident(g12,g0)
    c: PointOnObject(g12,g-1)
    c: Coincident(g13,g12)
    c: Vertical(g13)
    c: Coincident(g14,g13)
    c: Coincident(g15,g14)
    c: Coincident(g16,g15)
    c: Coincident(g16,g11)
    c: Vertical(g16)
    c: DistanceX(g15,g8) = 2.7
    c: DistanceY(g14,g1) = 2.7
    c: Parallel(g2,g15)
    c: DistanceX(g0,g13) = 2.7
    c: DistanceY(g12,g13) = 7.1
    c: Parallel(g1,g14)
FEATURE [PartDesign::Pad] Pad103
  BaseFeature = -> Pad102
  Direction = (0,0,1)
  Length = 1.5
  Length2 = 10
  Profile = -> Sketch173
  ReferenceAxis = -> Sketch173 [N_Axis]
  Refine = true
  Suppressed = false
  Type = 0
FEATURE [Sketcher::SketchObject] Sketch174
  ArcFitTolerance = 1e-06
  AttachmentSupport = -> [Pad103]
  ExternalGeometry = -> [Pad103]
  FullyConstrained = true
  MakeInternals = false
  MapMode = 5
  Placement = pos=(0,0,1.5) rot=(0,0,1;0rad)
  sketch-geometry (16):
    g0: LineSegment StartX=10.05 StartY=10.7528 StartZ=0 EndX=12.45 EndY=11.2148 EndZ=0
    g1: LineSegment StartX=12.45 StartY=11.2148 StartZ=0 EndX=12.45 EndY=0 EndZ=0
    g2: LineSegment StartX=10.05 StartY=10.7528 StartZ=0 EndX=10.05 EndY=0 EndZ=0
    g3: LineSegment StartX=12.45 StartY=0 StartZ=0 EndX=10.05 EndY=0 EndZ=0
    g4: LineSegment StartX=19.8 StartY=12.6295 StartZ=0 EndX=22.2 EndY=13.0915 EndZ=0
    g5: LineSegment StartX=19.8 StartY=12.6295 StartZ=0 EndX=19.8 EndY=0 EndZ=0
    g6: LineSegment StartX=22.2 StartY=13.0915 StartZ=0 EndX=22.2 EndY=0 EndZ=0
    g7: LineSegment StartX=22.2 StartY=0 StartZ=0 EndX=19.8 EndY=0 EndZ=0
    g8: LineSegment StartX=29.55 StartY=14.5063 StartZ=0 EndX=31.95 EndY=14.9682 EndZ=0
    g9: LineSegment StartX=31.95 StartY=14.9682 StartZ=0 EndX=31.95 EndY=0 EndZ=0
    g10: LineSegment StartX=29.55 StartY=14.5063 StartZ=0 EndX=29.55 EndY=0 EndZ=0
    g11: LineSegment StartX=29.55 StartY=0 StartZ=0 EndX=31.95 EndY=0 EndZ=0
    g12: LineSegment StartX=39.3 StartY=16.383 StartZ=0 EndX=41.7 EndY=16.845 EndZ=0
    g13: LineSegment StartX=41.7 StartY=16.845 StartZ=0 EndX=41.7 EndY=0 EndZ=0
    g14: LineSegment StartX=39.3 StartY=16.383 StartZ=0 EndX=39.3 EndY=0 EndZ=0
    g15: LineSegment StartX=39.3 StartY=0 StartZ=0 EndX=41.7 EndY=0 EndZ=0
  constraints (49):
    c: PointOnObject(g0,g-4)
    c: PointOnObject(g0,g-4)
    c: Coincident(g1,g0)
    c: PointOnObject(g1,g-3)
    c: Vertical(g1)
    c: Coincident(g2,g0)
    c: PointOnObject(g2,g-3)
    c: Vertical(g2)
    c: Coincident(g3,g1)
    c: Coincident(g3,g2)
    c: DistanceX(g3,g3) = 2.4
    c: PointOnObject(g4,g-4)
    c: PointOnObject(g4,g-4)
    c: Coincident(g5,g4)
    c: PointOnObject(g5,g-3)
    c: Vertical(g5)
    c: Coincident(g6,g4)
    c: PointOnObject(g6,g-3)
    c: Vertical(g6)
    c: Coincident(g7,g6)
    c: Coincident(g7,g5)
    c: DistanceX(g7,g7) = 2.4
    c: PointOnObject(g8,g-4)
    c: Coincident(g9,g8)
    c: PointOnObject(g9,g-3)
    c: Vertical(g9)
    c: Coincident(g10,g8)
    c: PointOnObject(g10,g-3)
    c: Vertical(g10)
    c: Coincident(g11,g10)
    c: Coincident(g11,g9)
    c: PointOnObject(g12,g-4)
    c: PointOnObject(g12,g-4)
    c: Coincident(g13,g12)
    c: PointOnObject(g13,g-3)
    c: Vertical(g13)
    c: Coincident(g14,g12)
    c: PointOnObject(g14,g-3)
    c: Vertical(g14)
    c: Coincident(g15,g14)
    c: Coincident(g15,g13)
    c: DistanceX(g15,g15) = 2.4
    c: DistanceX(g11,g11) = 2.4
    c: DistanceX(g-3,g2) = 7.35
    c: DistanceX(g1,g5) = 7.35
    c: DistanceX(g6,g10) = 7.35
    c: DistanceX(g9,g14) = 7.35
    c: DistanceX(g13,g-5) = 7.45553
    c: PointOnObject(g8,g-4)
FEATURE [PartDesign::Pad] Pad104
  BaseFeature = -> Pad103
  Direction = (0,0,1)
  Length = 1
  Length2 = 10
  Profile = -> Sketch174
  ReferenceAxis = -> Sketch174 [N_Axis]
  Refine = true
  Suppressed = false
  Type = 0
FEATURE [Sketcher::SketchObject] Sketch175
  ArcFitTolerance = 1e-06
  AttachmentSupport = -> [Pad104]
  ExternalGeometry = -> [Pad104]
  FullyConstrained = true
  MakeInternals = false
  MapMode = 5
  Placement = pos=(0,0,3) rot=(0,0,1;0rad)
  sketch-geometry (1):
    g0: Circle CenterX=48.6555 CenterY=21.9 CenterZ=0 NormalX=0 NormalY=0 NormalZ=1 AngleXU=0 Radius=1.6
  constraints (3):
    c: Diameter(g0) = 3.2
    c: DistanceX(g0,g-4) = 3.2
    c: DistanceY(g0,g-4) = 4
FEATURE [PartDesign::Pocket] Pocket077
  BaseFeature = -> Pad104
  Direction = (0,0,-1)
  Length = 1
  Length2 = 5
  Profile = -> Sketch175
  ReferenceAxis = -> Sketch175 [N_Axis]
  Refine = true
  Suppressed = false
  Type = 0
FEATURE [Sketcher::SketchObject] Sketch176
  ArcFitTolerance = 1e-06
  AttachmentSupport = -> [Pocket077]
  ExternalGeometry = -> [Pocket077]
  FullyConstrained = true
  MakeInternals = false
  MapMode = 5
  Placement = pos=(0,0,0) rot=(1,0,0;1.5708rad)
  sketch-geometry (4):
    g0: LineSegment StartX=0 StartY=0 StartZ=0 EndX=0 EndY=-16.5 EndZ=0
    g1: LineSegment StartX=0 StartY=-16.5 StartZ=0 EndX=33.7 EndY=-16.5 EndZ=0
    g2: LineSegment StartX=33.7 StartY=-16.5 StartZ=0 EndX=33.7 EndY=0 EndZ=0
    g3: LineSegment StartX=33.7 StartY=0 StartZ=0 EndX=0 EndY=0 EndZ=0
  constraints (11):
    c: Coincident(g0,g1)
    c: Coincident(g1,g2)
    c: Coincident(g2,g3)
    c: Coincident(g3,g0)
    c: Vertical(g0)
    c: Vertical(g2)
    c: Horizontal(g1)
    c: Horizontal(g3)
    c: Coincident(g0,g-1)
    c: DistanceY(g2,g2) = 16.5
    c: DistanceX(g1,g1) = 33.7
FEATURE [PartDesign::Pad] Pad105
  BaseFeature = -> Pocket077
  Direction = (0,-1,2e-16)
  Length = 1.5
  Length2 = 10
  Profile = -> Sketch176
  ReferenceAxis = -> Sketch176 [N_Axis]
  Refine = true
  Reversed = true
  Suppressed = false
  Type = 0
FEATURE [Sketcher::SketchObject] Sketch177
  ArcFitTolerance = 1e-06
  AttachmentSupport = -> [Pad105]
  ExternalGeometry = -> [Pad105]
  FullyConstrained = true
  MakeInternals = false
  MapMode = 5
  Placement = pos=(0,0,0) rot=(1,0,0;3.14159rad)
  sketch-geometry (7):
    g0: LineSegment StartX=33.7 StartY=-1.5 StartZ=0 EndX=46.3206 EndY=-20.6594 EndZ=0
    g1: LineSegment StartX=46.3206 StartY=-20.6594 StartZ=0 EndX=48.2845 EndY=-21.0375 EndZ=0
    g2: LineSegment StartX=48.2845 StartY=-21.0375 StartZ=0 EndX=48.4735 EndY=-20.0555 EndZ=0
    g3: LineSegment StartX=48.4735 StartY=-20.0555 StartZ=0 EndX=47.6094 EndY=-19.8891 EndZ=0
    g4: LineSegment StartX=47.6094 StartY=-19.8891 StartZ=0 EndX=34.5081 EndY=0 EndZ=0
    g5: LineSegment StartX=34.5081 StartY=0 StartZ=0 EndX=33.7 EndY=0 EndZ=0
    g6: LineSegment StartX=33.7 StartY=0 StartZ=0 EndX=33.7 EndY=-1.5 EndZ=0
  constraints (19):
    c: Coincident(g0,g-3)
    c: Coincident(g1,g0)
    c: Coincident(g2,g1)
    c: Coincident(g3,g2)
    c: Coincident(g4,g3)
    c: PointOnObject(g4,g-4)
    c: Coincident(g5,g4)
    c: Coincident(g5,g-4)
    c: Distance(g0,g4) = 1.5
    c: Parallel(g0,g4)
    c: Angle(g2,g1) = 1.5708
    c: Angle(g3,g2) = 1.5708
    c: Distance(g2) = 1
    c: Parallel(g-5,g1)
    c: Distance(g1) = 2
    c: Distance(g0,g-6) = 1.8
    c: Distance(g0,g-7) = 4.1
    c: Coincident(g6,g5)
    c: Coincident(g6,g0)
FEATURE [PartDesign::Pad] Pad106
  BaseFeature = -> Pad105
  Direction = (0,0,-1)
  Length = 16.5
  Length2 = 10
  Profile = -> Sketch177
  ReferenceAxis = -> Sketch177 [N_Axis]
  Refine = true
  Suppressed = false
  Type = 0
FEATURE [Sketcher::SketchObject] Sketch178
  ArcFitTolerance = 1e-06
  AttachmentSupport = -> [Pad106]
  ExternalGeometry = -> [Pad106]
  FullyConstrained = true
  MakeInternals = false
  MapMode = 5
  Placement = pos=(0,0,0) rot=(1,0,0;3.14159rad)
  sketch-geometry (11):
    g0: ArcOfCircle CenterX=50.8475 CenterY=-2.65774 CenterZ=0 NormalX=0 NormalY=0 NormalZ=1 AngleXU=0 Radius=3.3 StartAngle=5.02282 EndAngle=6.45301
    g1: LineSegment StartX=54.1 StartY=-2.1 StartZ=0 EndX=48.4404 EndY=-0.831343 EndZ=0
    g2: LineSegment StartX=48.4404 StartY=-0.831343 StartZ=0 EndX=45.4137 EndY=-16.5559 EndZ=0
    g3: LineSegment StartX=45.4137 StartY=-16.5559 StartZ=0 EndX=47.6094 EndY=-19.8891 EndZ=0
    g4: LineSegment StartX=47.6094 StartY=-19.8891 StartZ=0 EndX=48.4735 EndY=-20.0555 EndZ=0
    g5: LineSegment StartX=48.4735 StartY=-20.0555 StartZ=0 EndX=48.2845 EndY=-21.0375 EndZ=0
    g6: LineSegment StartX=48.2845 StartY=-21.0375 StartZ=0 EndX=46.3206 EndY=-20.6594 EndZ=0
    g7: LineSegment StartX=46.3206 StartY=-20.6594 StartZ=0 EndX=44.5555 EndY=-20.3063 EndZ=0
    g8: LineSegment StartX=44.5555 StartY=-20.3063 StartZ=0 EndX=45.5709 EndY=-24.6903 EndZ=0
    g9: LineSegment StartX=45.5709 StartY=-24.6903 StartZ=0 EndX=51.8555 EndY=-25.9 EndZ=0
    g10: LineSegment StartX=51.8555 StartY=-25.9 StartZ=0 EndX=51.8555 EndY=-5.8 EndZ=0
  constraints (24):
    c: Tangent(g0,g-4) = -1.5708
    c: Coincident(g2,g1)
    c: PointOnObject(g2,g-11)
    c: Coincident(g3,g2)
    c: Coincident(g3,g-11)
    c: Coincident(g4,g3)
    c: Coincident(g4,g-10)
    c: Coincident(g5,g4)
    c: Coincident(g5,g-9)
    c: Coincident(g6,g5)
    c: Coincident(g6,g-8)
    c: Coincident(g7,g6)
    c: Coincident(g7,g-7)
    c: Coincident(g8,g7)
    c: Coincident(g8,g-7)
    c: Coincident(g9,g8)
    c: Coincident(g9,g-6)
    c: Coincident(g10,g9)
    c: Coincident(g10,g-5)
    c: Coincident(g0,g10)
    c: Coincident(g0,g1)
    c: Tangent(g1,g-3) = 1.5708
    c: Distance(g1) = 5.8
    c: Angle(g2,g-12) = 1.5708
FEATURE [PartDesign::Pocket] Pocket078
  BaseFeature = -> Pad106
  Direction = (0,0,1)
  Length = 0.5
  Length2 = 5
  Profile = -> Sketch178
  ReferenceAxis = -> Sketch178 [N_Axis]
  Refine = true
  Suppressed = false
  Type = 0
FEATURE [Sketcher::SketchObject] Sketch179
  ArcFitTolerance = 1e-06
  AttachmentSupport = -> [Pocket078]
  ExternalGeometry = -> [Pocket078]
  FullyConstrained = true
  MakeInternals = false
  MapMode = 5
  Placement = pos=(0,1.5,0) rot=(0,0.707107,0.707107;3.14159rad)
  sketch-geometry (4):
    g0: LineSegment StartX=0 StartY=-16.5 StartZ=0 EndX=0 EndY=-5 EndZ=0
    g1: LineSegment StartX=0 StartY=-5 StartZ=0 EndX=-22.5 EndY=-5 EndZ=0
    g2: LineSegment StartX=-22.5 StartY=-5 StartZ=0 EndX=-22.5 EndY=-16.5 EndZ=0
    g3: LineSegment StartX=-22.5 StartY=-16.5 StartZ=0 EndX=0 EndY=-16.5 EndZ=0
  constraints (12):
    c: Coincident(g0,g1)
    c: Coincident(g1,g2)
    c: Coincident(g2,g3)
    c: Coincident(g3,g0)
    c: Vertical(g0)
    c: Vertical(g2)
    c: Horizontal(g1)
    c: Horizontal(g3)
    c: Coincident(g0,g-4)
    c: DistanceX(g1,g1) = 22.5
    c: DistanceY(g1,g-5) = 5
    c: DistanceY(g2,g2) = 11.5
FEATURE [PartDesign::Pocket] Pocket079
  BaseFeature = -> Pocket078
  Direction = (0,-1,2e-16)
  Length = 5
  Length2 = 5
  Profile = -> Sketch179
  ReferenceAxis = -> Sketch179 [N_Axis]
  Refine = true
  Suppressed = false
  Type = 0
FEATURE [Sketcher::SketchObject] Sketch180
  ArcFitTolerance = 1e-06
  AttachmentOffset = pos=(0,0,-5.3) rot=(0,0,1;0rad)
  AttachmentSupport = -> [Pocket079]
  ExternalGeometry = -> [Pocket079]
  FullyConstrained = true
  MakeInternals = false
  MapMode = 5
  Placement = pos=(0,0,-3.8) rot=(0,0,1;0rad)
  sketch-geometry (4):
    g0: LineSegment StartX=10 StartY=0 StartZ=0 EndX=11.05 EndY=-6.9208 EndZ=0
    g1: LineSegment StartX=16 StartY=0 StartZ=0 EndX=16.78 EndY=-5.14117 EndZ=0
    g2: LineSegment StartX=16 StartY=0 StartZ=0 EndX=10 EndY=0 EndZ=0
    g3: ArcOfCircle CenterX=13.915 CenterY=-6.03098 CenterZ=0 NormalX=0 NormalY=0 NormalZ=1 AngleXU=0 Radius=3 StartAngle=3.44273 EndAngle=6.58432
  constraints (14):
    c: PointOnObject(g0,g-4)
    c: PointOnObject(g1,g-3)
    c: Coincident(g2,g1)
    c: PointOnObject(g2,g0)
    c: Horizontal(g2)
    c: DistanceX(g-1,g0) = 10
    c: DistanceX(g2,g2) = 6
    c: Parallel(g1,g0)
    c: Coincident(g3,g0)
    c: Coincident(g3,g1)
    c: Diameter(g3) = 6
    c: Distance(g0) = 7
    c: Symmetric(g0,g1,g3)
    c: Distance(g1) = 5.2
FEATURE [PartDesign::Pad] Pad107
  BaseFeature = -> Pocket079
  Direction = (0,0,1)
  Length = 2.4
  Length2 = 10
  Profile = -> Sketch180
  ReferenceAxis = -> Sketch180 [N_Axis]
  Refine = true
  Reversed = true
  Suppressed = false
  Type = 0
FEATURE [Sketcher::SketchObject] Sketch181
  ArcFitTolerance = 1e-06
  AttachmentSupport = -> [Pad107]
  ExternalGeometry = -> [Pad107]
  FullyConstrained = true
  MakeInternals = false
  MapMode = 5
  Placement = pos=(0,0,-3.8) rot=(0,0,1;0rad)
  sketch-geometry (1):
    g0: Circle CenterX=13.915 CenterY=-6.03098 CenterZ=0 NormalX=0 NormalY=0 NormalZ=1 AngleXU=0 Radius=2.15
  constraints (2):
    c: Coincident(g0,g-3)
    c: Diameter(g0) = 4.3
FEATURE [PartDesign::Pad] Pad108
  BaseFeature = -> Pad107
  Direction = (0,0,1)
  Length = 2.3
  Length2 = 10
  Profile = -> Sketch181
  ReferenceAxis = -> Sketch181 [N_Axis]
  Refine = true
  Suppressed = false
  Type = 0
FEATURE [Sketcher::SketchObject] Sketch182
  ArcFitTolerance = 1e-06
  AttachmentSupport = -> [Pad108]
  ExternalGeometry = -> [Pad108]
  FullyConstrained = true
  MakeInternals = false
  MapMode = 5
  Placement = pos=(0,0,-1.5) rot=(0,0,1;0rad)
  sketch-geometry (1):
    g0: Circle CenterX=13.915 CenterY=-6.03098 CenterZ=0 NormalX=0 NormalY=0 NormalZ=1 AngleXU=0 Radius=1
  constraints (2):
    c: Coincident(g0,g-3)
    c: Diameter(g0) = 2
FEATURE [PartDesign::Pocket] Pocket080
  BaseFeature = -> Pad108
  Direction = (0,0,-1)
  Length = 5
  Length2 = 5
  Profile = -> Sketch182
  ReferenceAxis = -> Sketch182 [N_Axis]
  Refine = true
  Suppressed = false
  Type = 0
FEATURE [Sketcher::SketchObject] Sketch183
  ArcFitTolerance = 1e-06
  AttachmentOffset = pos=(0,0,-6) rot=(0,0,1;0rad)
  AttachmentSupport = -> [Pocket080]
  ExternalGeometry = -> [Pocket080]
  FullyConstrained = true
  MakeInternals = false
  MapMode = 5
  Placement = pos=(0,0,-4.5) rot=(0,0,1;0rad)
  sketch-geometry (4):
    g0: LineSegment StartX=21.3 StartY=0 StartZ=0 EndX=28.7 EndY=0 EndZ=0
    g1: LineSegment StartX=21.3 StartY=0 StartZ=0 EndX=23.055 EndY=-11.5676 EndZ=0
    g2: LineSegment StartX=28.7 StartY=0 StartZ=0 EndX=30.275 EndY=-10.3812 EndZ=0
    g3: ArcOfCircle CenterX=26.5753 CenterY=-10.4286 CenterZ=0 NormalX=0 NormalY=0 NormalZ=1 AngleXU=0 Radius=3.7 StartAngle=3.45453 EndAngle=6.29599
  constraints (13):
    c: PointOnObject(g0,g-1)
    c: Coincident(g1,g0)
    c: Coincident(g2,g0)
    c: Coincident(g3,g1)
    c: Coincident(g3,g2)
    c: Parallel(g1,g2)
    c: Distance(g0) = 7.4
    c: Distance(g1) = 11.7
    c: Diameter(g3) = 7.4
    c: PointOnObject(g0,g-1)
    c: Distance(g0,g-3) = 5.3
    c: Parallel(g-3,g1)
    c: Distance(g2) = 10.5
FEATURE [PartDesign::Pad] Pad109
  BaseFeature = -> Pocket080
  Direction = (0,0,1)
  Length = 2.5
  Length2 = 10
  Profile = -> Sketch183
  ReferenceAxis = -> Sketch183 [N_Axis]
  Refine = true
  Reversed = true
  Suppressed = false
  Type = 0
FEATURE [Sketcher::SketchObject] Sketch184
  ArcFitTolerance = 1e-06
  AttachmentSupport = -> [Pad109]
  ExternalGeometry = -> [Pad109]
  FullyConstrained = true
  MakeInternals = false
  MapMode = 5
  Placement = pos=(0,0,-4.5) rot=(0,0,1;0rad)
  sketch-geometry (1):
    g0: Circle CenterX=26.5753 CenterY=-10.4286 CenterZ=0 NormalX=0 NormalY=0 NormalZ=1 AngleXU=0 Radius=2.65
  constraints (2):
    c: Coincident(g0,g-3)
    c: Diameter(g0) = 5.3
FEATURE [PartDesign::Pad] Pad110
  BaseFeature = -> Pad109
  Direction = (0,0,1)
  Length = 2
  Length2 = 10
  Profile = -> Sketch184
  ReferenceAxis = -> Sketch184 [N_Axis]
  Refine = true
  Suppressed = false
  Type = 0
FEATURE [Sketcher::SketchObject] Sketch185
  ArcFitTolerance = 1e-06
  AttachmentSupport = -> [Pad110]
  ExternalGeometry = -> [Pad110]
  FullyConstrained = true
  MakeInternals = false
  MapMode = 5
  Placement = pos=(0,0,-2.5) rot=(0,0,1;0rad)
  sketch-geometry (1):
    g0: Circle CenterX=26.5753 CenterY=-10.4286 CenterZ=0 NormalX=0 NormalY=0 NormalZ=1 AngleXU=0 Radius=0.75
  constraints (2):
    c: Coincident(g0,g-3)
    c: Diameter(g0) = 1.5
FEATURE [PartDesign::Pocket] Pocket081
  BaseFeature = -> Pad110
  Direction = (0,0,-1)
  Length = 5
  Length2 = 5
  Profile = -> Sketch185
  ReferenceAxis = -> Sketch185 [N_Axis]
  Refine = true
  Suppressed = false
  Type = 0
FEATURE [Sketcher::SketchObject] Sketch186
  ArcFitTolerance = 1e-06
  AttachmentSupport = -> [Pocket081]
  ExternalGeometry = -> [Pocket081]
  FullyConstrained = true
  MakeInternals = false
  MapMode = 5
  Placement = pos=(0,0,0) rot=(0,0.707107,0.707107;3.14159rad)
  sketch-geometry (4):
    g0: LineSegment StartX=0 StartY=-5 StartZ=0 EndX=-22.5 EndY=-5 EndZ=0
    g1: LineSegment StartX=-22.5 StartY=-5 StartZ=0 EndX=-22.5 EndY=-6.2 EndZ=0
    g2: LineSegment StartX=-22.5 StartY=-6.2 StartZ=0 EndX=0 EndY=-6.2 EndZ=0
    g3: LineSegment StartX=0 StartY=-6.2 StartZ=0 EndX=0 EndY=-5 EndZ=0
  constraints (11):
    c: Coincident(g0,g1)
    c: Coincident(g1,g2)
    c: Coincident(g2,g3)
    c: Coincident(g3,g0)
    c: Horizontal(g0)
    c: Horizontal(g2)
    c: Vertical(g1)
    c: Vertical(g3)
    c: PointOnObject(g0,g-2)
    c: Coincident(g0,g-7)
    c: PointOnObject(g-3,g2)
FEATURE [PartDesign::Pad] Pad111
  BaseFeature = -> Pocket081
  Direction = (0,1,-2e-16)
  Length = 7.2
  Length2 = 10
  Profile = -> Sketch186
  ReferenceAxis = -> Sketch186 [N_Axis]
  Refine = true
  Suppressed = false
  Type = 0
FEATURE [Sketcher::SketchObject] Sketch187
  ArcFitTolerance = 1e-06
  AttachmentSupport = -> [Pad111]
  ExternalGeometry = -> [Pad111]
  FullyConstrained = true
  MakeInternals = false
  MapMode = 5
  Placement = pos=(0,0,-6.2) rot=(1,0,0;3.14159rad)
  sketch-geometry (3):
    g0: LineSegment StartX=22.5 StartY=-1.5 StartZ=0 EndX=22.5 EndY=-7.2 EndZ=0
    g1: LineSegment StartX=22.5 StartY=-7.2 StartZ=0 EndX=21.6349 EndY=-7.2 EndZ=0
    g2: LineSegment StartX=21.6349 StartY=-7.2 StartZ=0 EndX=22.5 EndY=-1.5 EndZ=0
  constraints (7):
    c: Coincident(g0,g-3)
    c: Coincident(g0,g-4)
    c: Coincident(g1,g0)
    c: PointOnObject(g1,g-4)
    c: Coincident(g2,g1)
    c: Coincident(g2,g0)
    c: Angle(g2,g0) = 0.150622
FEATURE [PartDesign::Pocket] Pocket082
  BaseFeature = -> Pad111
  Direction = (0,0,1)
  Length = 1.2
  Length2 = 5
  Profile = -> Sketch187
  ReferenceAxis = -> Sketch187 [N_Axis]
  Refine = true
  Suppressed = false
  Type = 0
FEATURE [Sketcher::SketchObject] Sketch188
  ArcFitTolerance = 1e-06
  AttachmentSupport = -> [Pocket082]
  ExternalGeometry = -> [Pocket082]
  FullyConstrained = true
  MakeInternals = false
  MapMode = 5
  Placement = pos=(0,1.5,0) rot=(0,0.707107,0.707107;3.14159rad)
  sketch-geometry (4):
    g0: LineSegment StartX=0 StartY=0 StartZ=0 EndX=-1.2 EndY=0 EndZ=0
    g1: LineSegment StartX=-1.2 StartY=0 StartZ=0 EndX=-1.2 EndY=-5 EndZ=0
    g2: LineSegment StartX=-1.2 StartY=-5 StartZ=0 EndX=0 EndY=-5 EndZ=0
    g3: LineSegment StartX=0 StartY=-5 StartZ=0 EndX=0 EndY=0 EndZ=0
  constraints (11):
    c: Coincident(g0,g1)
    c: Coincident(g1,g2)
    c: Coincident(g2,g3)
    c: Coincident(g3,g0)
    c: Horizontal(g0)
    c: Horizontal(g2)
    c: Vertical(g1)
    c: Vertical(g3)
    c: Coincident(g0,g-1)
    c: PointOnObject(g1,g-4)
    c: DistanceX(g2,g2) = 1.2
FEATURE [PartDesign::Pad] Pad112
  BaseFeature = -> Pocket082
  Direction = (0,1,-2e-16)
  Length = 5.7
  Length2 = 10
  Profile = -> Sketch188
  ReferenceAxis = -> Sketch188 [N_Axis]
  Refine = true
  Suppressed = false
  Type = 0
FEATURE [Sketcher::SketchObject] Sketch189
  ArcFitTolerance = 1e-06
  AttachmentSupport = -> [Pad112]
  ExternalGeometry = -> [Pad112]
  FullyConstrained = true
  MakeInternals = false
  MapMode = 5
  Placement = pos=(0,0,-6.2) rot=(1,0,0;3.14159rad)
  sketch-geometry (5):
    g0: LineSegment StartX=21.6349 StartY=-7.2 StartZ=0 EndX=22.5 EndY=-1.5 EndZ=0
    g1: LineSegment StartX=22.5 StartY=-1.5 StartZ=0 EndX=22.5 EndY=0 EndZ=0
    g2: LineSegment StartX=22.5 StartY=0 StartZ=0 EndX=21.3 EndY=1.4e-15 EndZ=0
    g3: LineSegment StartX=21.3 StartY=1.4e-15 StartZ=0 EndX=20.2072 EndY=-7.2 EndZ=0
    g4: LineSegment StartX=20.2072 StartY=-7.2 StartZ=0 EndX=21.6349 EndY=-7.2 EndZ=0
  constraints (11):
    c: Coincident(g0,g-4)
    c: Coincident(g0,g-5)
    c: Coincident(g1,g0)
    c: Coincident(g1,g-6)
    c: Coincident(g2,g1)
    c: Coincident(g2,g-6)
    c: Coincident(g3,g2)
    c: PointOnObject(g3,g-3)
    c: Coincident(g4,g3)
    c: Coincident(g4,g0)
    c: Parallel(g0,g3)
FEATURE [PartDesign::Pad] Pad113
  BaseFeature = -> Pad112
  Direction = (0,0,-1)
  Length = 10.3
  Length2 = 10
  Profile = -> Sketch189
  ReferenceAxis = -> Sketch189 [N_Axis]
  Refine = true
  Suppressed = false
  Type = 0
FEATURE [Sketcher::SketchObject] Sketch190
  ArcFitTolerance = 1e-06
  AttachmentSupport = -> [Pad113]
  ExternalGeometry = -> [Pad113]
  FullyConstrained = true
  MakeInternals = false
  MapMode = 5
  Placement = pos=(0,7.2,0) rot=(0,0.707107,0.707107;3.14159rad)
  sketch-geometry (4):
    g0: LineSegment StartX=0 StartY=-6.2 StartZ=0 EndX=-21.6349 EndY=-6.2 EndZ=0
    g1: LineSegment StartX=-21.6349 StartY=-6.2 StartZ=0 EndX=-21.6349 EndY=-16.5 EndZ=0
    g2: LineSegment StartX=-21.6349 StartY=-16.5 StartZ=0 EndX=0 EndY=-16.5 EndZ=0
    g3: LineSegment StartX=0 StartY=-16.5 StartZ=0 EndX=0 EndY=-6.2 EndZ=0
  constraints (10):
    c: Coincident(g0,g1)
    c: Coincident(g1,g2)
    c: Coincident(g2,g3)
    c: Coincident(g3,g0)
    c: Horizontal(g0)
    c: Horizontal(g2)
    c: Vertical(g1)
    c: Vertical(g3)
    c: Coincident(g0,g-3)
    c: Coincident(g1,g-5)
FEATURE [PartDesign::Pad] Pad114
  BaseFeature = -> Pad113
  Direction = (0,1,-2e-16)
  Length = 1.5
  Length2 = 10
  Profile = -> Sketch190
  ReferenceAxis = -> Sketch190 [N_Axis]
  Refine = true
  Reversed = true
  Suppressed = false
  Type = 0
FEATURE [Sketcher::SketchObject] Sketch191
  ArcFitTolerance = 1e-06
  AttachmentSupport = -> [Pad114]
  ExternalGeometry = -> [Pad114]
  FullyConstrained = true
  MakeInternals = false
  MapMode = 5
  Placement = pos=(0,0,-16.5) rot=(1,0,0;3.14159rad)
  sketch-geometry (4):
    g0: LineSegment StartX=21.3 StartY=0 StartZ=0 EndX=20.4349 EndY=-5.7 EndZ=0
    g1: LineSegment StartX=20.4349 StartY=-5.7 StartZ=0 EndX=0 EndY=-5.7 EndZ=0
    g2: LineSegment StartX=0 StartY=-5.7 StartZ=0 EndX=0 EndY=0 EndZ=0
    g3: LineSegment StartX=0 StartY=0 StartZ=0 EndX=21.3 EndY=0 EndZ=0
  constraints (8):
    c: Coincident(g0,g-3)
    c: Coincident(g0,g-4)
    c: Coincident(g1,g0)
    c: Coincident(g1,g-4)
    c: Coincident(g2,g1)
    c: Coincident(g2,g-1)
    c: Coincident(g3,g2)
    c: Coincident(g3,g0)
FEATURE [PartDesign::Pad] Pad115
  BaseFeature = -> Pad114
  Direction = (0,0,-1)
  Length = 1.2
  Length2 = 10
  Profile = -> Sketch191
  ReferenceAxis = -> Sketch191 [N_Axis]
  Refine = true
  Reversed = true
  Suppressed = false
  Type = 0
FEATURE [Sketcher::SketchObject] Sketch192
  ArcFitTolerance = 1e-06
  AttachmentSupport = -> [Pad115]
  ExternalGeometry = -> [Pad115]
  FullyConstrained = true
  MakeInternals = false
  MapMode = 5
  Placement = pos=(0,0,0) rot=(0.57735,-0.57735,-0.57735;2.0944rad)
  sketch-geometry (6):
    g0: LineSegment StartX=-5.7 StartY=-15.3 StartZ=0 EndX=-3.5 EndY=-15.3 EndZ=0
    g1: LineSegment StartX=-5.7 StartY=-15.3 StartZ=0 EndX=-5.7 EndY=-6.2 EndZ=0
    g2: LineSegment StartX=-5.7 StartY=-6.2 StartZ=0 EndX=9e-16 EndY=-6.2 EndZ=0
    g3: LineSegment StartX=9e-16 StartY=-6.2 StartZ=0 EndX=9e-16 EndY=-7.3 EndZ=0
    g4: LineSegment StartX=9e-16 StartY=-7.3 StartZ=0 EndX=-3.5 EndY=-7.3 EndZ=0
    g5: LineSegment StartX=-3.5 StartY=-7.3 StartZ=0 EndX=-3.5 EndY=-15.3 EndZ=0
  constraints (17):
    c: DistanceY(g-4,g-4) = 9.1
    c: Coincident(g0,g-5)
    c: PointOnObject(g0,g-5)
    c: Coincident(g1,g0)
    c: Coincident(g1,g-4)
    c: Coincident(g2,g1)
    c: Coincident(g3,g2)
    c: Vertical(g3)
    c: Coincident(g4,g3)
    c: Horizontal(g4)
    c: Coincident(g5,g4)
    c: Coincident(g5,g0)
    c: Vertical(g5)
    c: DistanceY(g3,g3) = 1.1
    c: Coincident(g2,g-3)
    c: DistanceX(g0,g0) = 2.2
    c: DistanceX(g-5,g-5) = 5.7
FEATURE [PartDesign::Pad] Pad116
  BaseFeature = -> Pad115
  Direction = (-1,0,0)
  Length = 1.5
  Length2 = 10
  Profile = -> Sketch192
  ReferenceAxis = -> Sketch192 [N_Axis]
  Refine = true
  Reversed = true
  Suppressed = false
  Type = 0
FEATURE [Sketcher::SketchObject] Sketch193
  ArcFitTolerance = 1e-06
  AttachmentSupport = -> [Pad116]
  ExternalGeometry = -> [Pad116]
  FullyConstrained = true
  MakeInternals = false
  MapMode = 5
  Placement = pos=(0,0,-16.5) rot=(1,0,0;3.14159rad)
  sketch-geometry (4):
    g0: ArcOfCircle CenterX=13.915 CenterY=6.03098 CenterZ=0 NormalX=0 NormalY=0 NormalZ=1 AngleXU=0 Radius=3 StartAngle=5.98205 EndAngle=9.12364
    g1: LineSegment StartX=11.05 StartY=6.9208 StartZ=0 EndX=8.90764 EndY=-7.2 EndZ=0
    g2: LineSegment StartX=16.78 StartY=5.14117 StartZ=0 EndX=14.9076 EndY=-7.2 EndZ=0
    g3: LineSegment StartX=14.9076 StartY=-7.2 StartZ=0 EndX=8.90764 EndY=-7.2 EndZ=0
  constraints (10):
    c: Tangent(g0,g-5) = -1.5708
    c: Coincident(g0,g-5)
    c: Coincident(g1,g0)
    c: PointOnObject(g1,g-6)
    c: Coincident(g2,g0)
    c: PointOnObject(g2,g-6)
    c: Coincident(g3,g2)
    c: Coincident(g3,g1)
    c: PointOnObject(g-4,g1)
    c: PointOnObject(g-3,g2)
FEATURE [PartDesign::Pad] Pad117
  BaseFeature = -> Pad116
  Direction = (0,0,-1)
  Length = 3.5
  Length2 = 10
  Profile = -> Sketch193
  ReferenceAxis = -> Sketch193 [N_Axis]
  Refine = true
  Reversed = true
  Suppressed = false
  Type = 0
FEATURE [PartDesign::Body] Body004  label="Right_Foot"
  AllowCompound = false
  Group = -> [Sketch172,Pad102,Sketch173,Pad103,Sketch174,Pad104,Sketch175,Pocket077,Sketch176,Pad105,Sketch177,Pad106,Sketch178,Pocket078,Sketch179,Pocket079,Sketch180,Pad107,Sketch181,Pad108,Sketch182,Pocket080,Sketch183,Pad109,Sketch184,Pad110,Sketch185,Pocket081,Sketch186,Pad111,Sketch187,Pocket082,Sketch188,Pad112,Sketch189,Pad113,Sketch190,Pad114,Sketch191,Pad115,Sketch192,Pad116,Sketch193,Pad117,+35 more]
  Origin = -> Origin004
  Placement = pos=(-74.7938,-16.5,12.9107) rot=(-0.995146,-0.069587,0.069587;4.70752rad)
  Tip = -> Pocket185
COMPONENT P5 — recipe-attached ("Pre_Left_Foot", modeled in this document).
Construction recipe (the document's own serialized feature program — sketch geometry with constraints, then the solid features built on it; lengths are millimeters unless a unit is written):

FEATURE [Sketcher::SketchObject] Sketch203
  ArcFitTolerance = 1e-06
  AttachmentSupport = -> [XY_Plane005]
  FullyConstrained = true
  MakeInternals = false
  MapMode = 5
  sketch-geometry (14):
    g0: LineSegment StartX=0 StartY=0 StartZ=0 EndX=43 EndY=0 EndZ=0
    g1: ArcOfCircle CenterX=50.8475 CenterY=2.65774 CenterZ=0 NormalX=0 NormalY=0 NormalZ=1 AngleXU=0 Radius=3.3 StartAngle=6.11336 EndAngle=7.54355
    g2: LineSegment StartX=51.8555 StartY=5.8 StartZ=0 EndX=51.8555 EndY=25.9 EndZ=0
    g3: LineSegment StartX=51.8555 StartY=25.9 StartZ=0 EndX=45.5709 EndY=24.6903 EndZ=0
    g4: LineSegment StartX=45.5709 StartY=24.6903 StartZ=0 EndX=44.5555 EndY=20.3063 EndZ=0
    g5: LineSegment StartX=44.5555 StartY=20.3063 StartZ=0 EndX=34.343 EndY=18.3406 EndZ=0
    g6: LineSegment StartX=34.343 StartY=18.3406 StartZ=0 EndX=33.8894 EndY=20.6973 EndZ=0
    g7: LineSegment StartX=33.8894 StartY=20.6973 StartZ=0 EndX=31.5326 EndY=20.2437 EndZ=0
    g8: LineSegment StartX=31.5326 StartY=20.2437 StartZ=0 EndX=31.9863 EndY=17.8869 EndZ=0
    g9: LineSegment StartX=31.9863 StartY=17.8869 StartZ=0 EndX=4 EndY=12.5 EndZ=0
    g10: LineSegment StartX=4 StartY=12.5 StartZ=0 EndX=0 EndY=8 EndZ=0
    g11: LineSegment StartX=0 StartY=8 StartZ=0 EndX=0 EndY=0 EndZ=0
    g12: ArcOfCircle CenterX=43 CenterY=15.82 CenterZ=0 NormalX=0 NormalY=0 NormalZ=1 AngleXU=0 Radius=15.82 StartAngle=4.71239 EndAngle=4.90962
    g13: LineSegment StartX=46.1 StartY=0.306702 StartZ=0 EndX=54.1 EndY=2.1 EndZ=0
  constraints (44):
    c: Coincident(g0,g-1)
    c: Coincident(g2,g1)
    c: Vertical(g2)
    c: Coincident(g3,g2)
    c: Coincident(g4,g3)
    c: Coincident(g5,g4)
    c: Coincident(g6,g5)
    c: Coincident(g7,g6)
    c: Coincident(g8,g7)
    c: Coincident(g10,g9)
    c: PointOnObject(g10,g-2)
    c: Coincident(g11,g10)
    c: Coincident(g11,g0)
    c: Parallel(g7,g5)
    c: Parallel(g3,g5)
    c: Parallel(g7,g9)
    c: Distance(g7) = 2.4
    c: Distance(g5) = 10.4
    c: Angle(g5,g6) = 1.5708
    c: Angle(g8,g9) = 1.5708
    c: Distance(g3) = 6.4
    c: DistanceY(g11,g11) = 8
    c: Distance(g8) = 2.4
    c: Distance(g6) = 2.4
    c: Coincident(g9,g8)
    c: Distance(g4) = 4.5
    c: DistanceX(g4,g2) = 7.3
    c: DistanceX(g0,g9) = 4
    c: DistanceY(g0,g9) = 12.5
    c: Distance(g9) = 28.5
    c: DistanceY(g0,g2) = 25.9
    c: DistanceX(g0,g1) = 54.1
    c: DistanceX(g0,g1) = 51.8555
    c: DistanceY(g1,g2) = 20.1
    c: PointOnObject(g0,g-1)
    c: Coincident(g12,g0)
    c: Coincident(g13,g12)
    c: Coincident(g13,g1)
    c: Tangent(g12,g-1)
    c: DistanceY(g1,g1) = 3.7
    c: Radius(g1) = 3.3
    c: DistanceX(g0,g0) = 43
    c: DistanceX(g12,g1) = 8
    c: Radius(g12) = 15.82
FEATURE [PartDesign::Pad] Pad123
  Direction = (0,0,1)
  Length = 1.5
  Length2 = 10
  Profile = -> Sketch203
  ReferenceAxis = -> Sketch203 [N_Axis]
  Refine = true
  Suppressed = false
  Type = 0
FEATURE [Sketcher::SketchObject] Sketch204
  ArcFitTolerance = 1e-06
  AttachmentSupport = -> [Pad123]
  ExternalGeometry = -> [Pad123]
  FullyConstrained = true
  MakeInternals = false
  MapMode = 5
  Placement = pos=(0,0,1.5) rot=(0,0,1;0rad)
  sketch-geometry (17):
    g0: LineSegment StartX=0 StartY=0 StartZ=0 EndX=0 EndY=8 EndZ=0
    g1: LineSegment StartX=0 StartY=8 StartZ=0 EndX=4 EndY=12.5 EndZ=0
    g2: LineSegment StartX=4 StartY=12.5 StartZ=0 EndX=31.9863 EndY=17.8869 EndZ=0
    g3: LineSegment StartX=31.9863 StartY=17.8869 StartZ=0 EndX=31.5326 EndY=20.2437 EndZ=0
    g4: LineSegment StartX=31.5326 StartY=20.2437 StartZ=0 EndX=33.8894 EndY=20.6973 EndZ=0
    g5: LineSegment StartX=33.8894 StartY=20.6973 StartZ=0 EndX=34.343 EndY=18.3406 EndZ=0
    g6: LineSegment StartX=34.343 StartY=18.3406 StartZ=0 EndX=44.5555 EndY=20.3063 EndZ=0
    g7: LineSegment StartX=44.5555 StartY=20.3063 StartZ=0 EndX=45.5709 EndY=24.6903 EndZ=0
    g8: LineSegment StartX=45.5709 StartY=24.6903 StartZ=0 EndX=51.8555 EndY=25.9 EndZ=0
    g9: LineSegment StartX=51.8555 StartY=25.9 StartZ=0 EndX=51.8555 EndY=5.8 EndZ=0
    g10: ArcOfCircle CenterX=50.8475 CenterY=2.65774 CenterZ=0 NormalX=0 NormalY=0 NormalZ=1 AngleXU=0 Radius=3.3 StartAngle=6.11336 EndAngle=7.54355
    g11: LineSegment StartX=54.1 StartY=2.1 StartZ=0 EndX=49.1555 EndY=0.991637 EndZ=0
    g12: LineSegment StartX=0 StartY=0 StartZ=0 EndX=2.7 EndY=0 EndZ=0
    g13: LineSegment StartX=2.7 StartY=0 StartZ=0 EndX=2.7 EndY=7.1 EndZ=0
    g14: LineSegment StartX=2.7 StartY=7.1 StartZ=0 EndX=5.1 EndY=9.8 EndZ=0
    g15: LineSegment StartX=5.1 StartY=9.8 StartZ=0 EndX=49.1555 EndY=18.28 EndZ=0
    g16: LineSegment StartX=49.1555 StartY=18.28 StartZ=0 EndX=49.1555 EndY=0.991637 EndZ=0
  constraints (40):
    c: Coincident(g0,g-1)
    c: Coincident(g0,g-12)
    c: Coincident(g1,g0)
    c: Coincident(g1,g-11)
    c: Coincident(g2,g1)
    c: Coincident(g2,g-10)
    c: Coincident(g3,g2)
    c: Coincident(g3,g-9)
    c: Coincident(g4,g3)
    c: Coincident(g4,g-8)
    c: Coincident(g5,g4)
    c: Coincident(g5,g-7)
    c: Coincident(g6,g5)
    c: Coincident(g6,g-6)
    c: Coincident(g7,g6)
    c: Coincident(g7,g-5)
    c: Coincident(g8,g7)
    c: Coincident(g8,g-4)
    c: Coincident(g9,g8)
    c: Coincident(g9,g-13)
    c: Coincident(g10,g9)
    c: Coincident(g10,g-14)
    c: Tangent(g10,g-13)
    c: Coincident(g11,g10)
    c: PointOnObject(g11,g-14)
    c: Coincident(g12,g0)
    c: PointOnObject(g12,g-1)
    c: Coincident(g13,g12)
    c: Vertical(g13)
    c: Coincident(g14,g13)
    c: Coincident(g15,g14)
    c: Coincident(g16,g15)
    c: Coincident(g16,g11)
    c: Vertical(g16)
    c: DistanceX(g15,g8) = 2.7
    c: DistanceY(g14,g1) = 2.7
    c: Parallel(g2,g15)
    c: DistanceX(g0,g13) = 2.7
    c: DistanceY(g12,g13) = 7.1
    c: Parallel(g1,g14)
FEATURE [PartDesign::Pad] Pad124
  BaseFeature = -> Pad123
  Direction = (0,0,1)
  Length = 1.5
  Length2 = 10
  Profile = -> Sketch204
  ReferenceAxis = -> Sketch204 [N_Axis]
  Refine = true
  Suppressed = false
  Type = 0
FEATURE [Sketcher::SketchObject] Sketch205
  ArcFitTolerance = 1e-06
  AttachmentSupport = -> [Pad124]
  ExternalGeometry = -> [Pad124]
  FullyConstrained = true
  MakeInternals = false
  MapMode = 5
  Placement = pos=(0,0,1.5) rot=(0,0,1;0rad)
  sketch-geometry (16):
    g0: LineSegment StartX=10.05 StartY=10.7528 StartZ=0 EndX=12.45 EndY=11.2148 EndZ=0
    g1: LineSegment StartX=12.45 StartY=11.2148 StartZ=0 EndX=12.45 EndY=0 EndZ=0
    g2: LineSegment StartX=10.05 StartY=10.7528 StartZ=0 EndX=10.05 EndY=0 EndZ=0
    g3: LineSegment StartX=12.45 StartY=0 StartZ=0 EndX=10.05 EndY=0 EndZ=0
    g4: LineSegment StartX=19.8 StartY=12.6295 StartZ=0 EndX=22.2 EndY=13.0915 EndZ=0
    g5: LineSegment StartX=19.8 StartY=12.6295 StartZ=0 EndX=19.8 EndY=0 EndZ=0
    g6: LineSegment StartX=22.2 StartY=13.0915 StartZ=0 EndX=22.2 EndY=0 EndZ=0
    g7: LineSegment StartX=22.2 StartY=0 StartZ=0 EndX=19.8 EndY=0 EndZ=0
    g8: LineSegment StartX=29.55 StartY=14.5063 StartZ=0 EndX=31.95 EndY=14.9682 EndZ=0
    g9: LineSegment StartX=31.95 StartY=14.9682 StartZ=0 EndX=31.95 EndY=0 EndZ=0
    g10: LineSegment StartX=29.55 StartY=14.5063 StartZ=0 EndX=29.55 EndY=0 EndZ=0
    g11: LineSegment StartX=29.55 StartY=0 StartZ=0 EndX=31.95 EndY=0 EndZ=0
    g12: LineSegment StartX=39.3 StartY=16.383 StartZ=0 EndX=41.7 EndY=16.845 EndZ=0
    g13: LineSegment StartX=41.7 StartY=16.845 StartZ=0 EndX=41.7 EndY=0 EndZ=0
    g14: LineSegment StartX=39.3 StartY=16.383 StartZ=0 EndX=39.3 EndY=0 EndZ=0
    g15: LineSegment StartX=39.3 StartY=0 StartZ=0 EndX=41.7 EndY=0 EndZ=0
  constraints (49):
    c: PointOnObject(g0,g-4)
    c: PointOnObject(g0,g-4)
    c: Coincident(g1,g0)
    c: PointOnObject(g1,g-3)
    c: Vertical(g1)
    c: Coincident(g2,g0)
    c: PointOnObject(g2,g-3)
    c: Vertical(g2)
    c: Coincident(g3,g1)
    c: Coincident(g3,g2)
    c: DistanceX(g3,g3) = 2.4
    c: PointOnObject(g4,g-4)
    c: PointOnObject(g4,g-4)
    c: Coincident(g5,g4)
    c: PointOnObject(g5,g-3)
    c: Vertical(g5)
    c: Coincident(g6,g4)
    c: PointOnObject(g6,g-3)
    c: Vertical(g6)
    c: Coincident(g7,g6)
    c: Coincident(g7,g5)
    c: DistanceX(g7,g7) = 2.4
    c: PointOnObject(g8,g-4)
    c: Coincident(g9,g8)
    c: PointOnObject(g9,g-3)
    c: Vertical(g9)
    c: Coincident(g10,g8)
    c: PointOnObject(g10,g-3)
    c: Vertical(g10)
    c: Coincident(g11,g10)
    c: Coincident(g11,g9)
    c: PointOnObject(g12,g-4)
    c: PointOnObject(g12,g-4)
    c: Coincident(g13,g12)
    c: PointOnObject(g13,g-3)
    c: Vertical(g13)
    c: Coincident(g14,g12)
    c: PointOnObject(g14,g-3)
    c: Vertical(g14)
    c: Coincident(g15,g14)
    c: Coincident(g15,g13)
    c: DistanceX(g15,g15) = 2.4
    c: DistanceX(g11,g11) = 2.4
    c: DistanceX(g-3,g2) = 7.35
    c: DistanceX(g1,g5) = 7.35
    c: DistanceX(g6,g10) = 7.35
    c: DistanceX(g9,g14) = 7.35
    c: DistanceX(g13,g-5) = 7.45553
    c: PointOnObject(g8,g-4)
FEATURE [PartDesign::Pad] Pad125
  BaseFeature = -> Pad124
  Direction = (0,0,1)
  Length = 1
  Length2 = 10
  Profile = -> Sketch205
  ReferenceAxis = -> Sketch205 [N_Axis]
  Refine = true
  Suppressed = false
  Type = 0
FEATURE [Sketcher::SketchObject] Sketch206
  ArcFitTolerance = 1e-06
  AttachmentSupport = -> [Pad125]
  ExternalGeometry = -> [Pad125]
  FullyConstrained = true
  MakeInternals = false
  MapMode = 5
  Placement = pos=(0,0,3) rot=(0,0,1;0rad)
  sketch-geometry (1):
    g0: Circle CenterX=48.6555 CenterY=21.9 CenterZ=0 NormalX=0 NormalY=0 NormalZ=1 AngleXU=0 Radius=1.6
  constraints (3):
    c: Diameter(g0) = 3.2
    c: DistanceX(g0,g-4) = 3.2
    c: DistanceY(g0,g-4) = 4
FEATURE [PartDesign::Pocket] Pocket087
  BaseFeature = -> Pad125
  Direction = (0,0,-1)
  Length = 1
  Length2 = 5
  Profile = -> Sketch206
  ReferenceAxis = -> Sketch206 [N_Axis]
  Refine = true
  Suppressed = false
  Type = 0
FEATURE [Sketcher::SketchObject] Sketch207
  ArcFitTolerance = 1e-06
  AttachmentSupport = -> [Pocket087]
  ExternalGeometry = -> [Pocket087]
  FullyConstrained = true
  MakeInternals = false
  MapMode = 5
  Placement = pos=(0,0,0) rot=(1,0,0;1.5708rad)
  sketch-geometry (4):
    g0: LineSegment StartX=0 StartY=0 StartZ=0 EndX=0 EndY=-16.5 EndZ=0
    g1: LineSegment StartX=0 StartY=-16.5 StartZ=0 EndX=33.7 EndY=-16.5 EndZ=0
    g2: LineSegment StartX=33.7 StartY=-16.5 StartZ=0 EndX=33.7 EndY=0 EndZ=0
    g3: LineSegment StartX=33.7 StartY=0 StartZ=0 EndX=0 EndY=0 EndZ=0
  constraints (11):
    c: Coincident(g0,g1)
    c: Coincident(g1,g2)
    c: Coincident(g2,g3)
    c: Coincident(g3,g0)
    c: Vertical(g0)
    c: Vertical(g2)
    c: Horizontal(g1)
    c: Horizontal(g3)
    c: Coincident(g0,g-1)
    c: DistanceY(g2,g2) = 16.5
    c: DistanceX(g1,g1) = 33.7
FEATURE [PartDesign::Pad] Pad126
  BaseFeature = -> Pocket087
  Direction = (0,-1,2e-16)
  Length = 1.5
  Length2 = 10
  Profile = -> Sketch207
  ReferenceAxis = -> Sketch207 [N_Axis]
  Refine = true
  Reversed = true
  Suppressed = false
  Type = 0
FEATURE [Sketcher::SketchObject] Sketch208
  ArcFitTolerance = 1e-06
  AttachmentSupport = -> [Pad126]
  ExternalGeometry = -> [Pad126]
  FullyConstrained = true
  MakeInternals = false
  MapMode = 5
  Placement = pos=(0,0,0) rot=(1,0,0;3.14159rad)
  sketch-geometry (7):
    g0: LineSegment StartX=33.7 StartY=-1.5 StartZ=0 EndX=46.3206 EndY=-20.6594 EndZ=0
    g1: LineSegment StartX=46.3206 StartY=-20.6594 StartZ=0 EndX=48.2845 EndY=-21.0375 EndZ=0
    g2: LineSegment StartX=48.2845 StartY=-21.0375 StartZ=0 EndX=48.4735 EndY=-20.0555 EndZ=0
    g3: LineSegment StartX=48.4735 StartY=-20.0555 StartZ=0 EndX=47.6094 EndY=-19.8891 EndZ=0
    g4: LineSegment StartX=47.6094 StartY=-19.8891 StartZ=0 EndX=34.5081 EndY=0 EndZ=0
    g5: LineSegment StartX=34.5081 StartY=0 StartZ=0 EndX=33.7 EndY=0 EndZ=0
    g6: LineSegment StartX=33.7 StartY=0 StartZ=0 EndX=33.7 EndY=-1.5 EndZ=0
  constraints (19):
    c: Coincident(g0,g-3)
    c: Coincident(g1,g0)
    c: Coincident(g2,g1)
    c: Coincident(g3,g2)
    c: Coincident(g4,g3)
    c: PointOnObject(g4,g-4)
    c: Coincident(g5,g4)
    c: Coincident(g5,g-4)
    c: Distance(g0,g4) = 1.5
    c: Parallel(g0,g4)
    c: Angle(g2,g1) = 1.5708
    c: Angle(g3,g2) = 1.5708
    c: Distance(g2) = 1
    c: Parallel(g-5,g1)
    c: Distance(g1) = 2
    c: Distance(g0,g-6) = 1.8
    c: Distance(g0,g-7) = 4.1
    c: Coincident(g6,g5)
    c: Coincident(g6,g0)
FEATURE [PartDesign::Pad] Pad127
  BaseFeature = -> Pad126
  Direction = (0,0,-1)
  Length = 16.5
  Length2 = 10
  Profile = -> Sketch208
  ReferenceAxis = -> Sketch208 [N_Axis]
  Refine = true
  Suppressed = false
  Type = 0
FEATURE [Sketcher::SketchObject] Sketch209
  ArcFitTolerance = 1e-06
  AttachmentSupport = -> [Pad127]
  ExternalGeometry = -> [Pad127]
  FullyConstrained = true
  MakeInternals = false
  MapMode = 5
  Placement = pos=(0,0,0) rot=(1,0,0;3.14159rad)
  sketch-geometry (11):
    g0: ArcOfCircle CenterX=50.8475 CenterY=-2.65774 CenterZ=0 NormalX=0 NormalY=0 NormalZ=1 AngleXU=0 Radius=3.3 StartAngle=5.02282 EndAngle=6.45301
    g1: LineSegment StartX=54.1 StartY=-2.1 StartZ=0 EndX=48.4404 EndY=-0.831343 EndZ=0
    g2: LineSegment StartX=48.4404 StartY=-0.831343 StartZ=0 EndX=45.4137 EndY=-16.5559 EndZ=0
    g3: LineSegment StartX=45.4137 StartY=-16.5559 StartZ=0 EndX=47.6094 EndY=-19.8891 EndZ=0
    g4: LineSegment StartX=47.6094 StartY=-19.8891 StartZ=0 EndX=48.4735 EndY=-20.0555 EndZ=0
    g5: LineSegment StartX=48.4735 StartY=-20.0555 StartZ=0 EndX=48.2845 EndY=-21.0375 EndZ=0
    g6: LineSegment StartX=48.2845 StartY=-21.0375 StartZ=0 EndX=46.3206 EndY=-20.6594 EndZ=0
    g7: LineSegment StartX=46.3206 StartY=-20.6594 StartZ=0 EndX=44.5555 EndY=-20.3063 EndZ=0
    g8: LineSegment StartX=44.5555 StartY=-20.3063 StartZ=0 EndX=45.5709 EndY=-24.6903 EndZ=0
    g9: LineSegment StartX=45.5709 StartY=-24.6903 StartZ=0 EndX=51.8555 EndY=-25.9 EndZ=0
    g10: LineSegment StartX=51.8555 StartY=-25.9 StartZ=0 EndX=51.8555 EndY=-5.8 EndZ=0
  constraints (24):
    c: Tangent(g0,g-4) = -1.5708
    c: Coincident(g2,g1)
    c: PointOnObject(g2,g-11)
    c: Coincident(g3,g2)
    c: Coincident(g3,g-11)
    c: Coincident(g4,g3)
    c: Coincident(g4,g-10)
    c: Coincident(g5,g4)
    c: Coincident(g5,g-9)
    c: Coincident(g6,g5)
    c: Coincident(g6,g-8)
    c: Coincident(g7,g6)
    c: Coincident(g7,g-7)
    c: Coincident(g8,g7)
    c: Coincident(g8,g-7)
    c: Coincident(g9,g8)
    c: Coincident(g9,g-6)
    c: Coincident(g10,g9)
    c: Coincident(g10,g-5)
    c: Coincident(g0,g10)
    c: Coincident(g0,g1)
    c: Tangent(g1,g-3) = 1.5708
    c: Distance(g1) = 5.8
    c: Angle(g2,g-12) = 1.5708
FEATURE [PartDesign::Pocket] Pocket088
  BaseFeature = -> Pad127
  Direction = (0,0,1)
  Length = 0.5
  Length2 = 5
  Profile = -> Sketch209
  ReferenceAxis = -> Sketch209 [N_Axis]
  Refine = true
  Suppressed = false
  Type = 0
FEATURE [Sketcher::SketchObject] Sketch210
  ArcFitTolerance = 1e-06
  AttachmentSupport = -> [Pocket088]
  ExternalGeometry = -> [Pocket088]
  FullyConstrained = true
  MakeInternals = false
  MapMode = 5
  Placement = pos=(0,1.5,0) rot=(0,0.707107,0.707107;3.14159rad)
  sketch-geometry (4):
    g0: LineSegment StartX=0 StartY=-16.5 StartZ=0 EndX=0 EndY=-5 EndZ=0
    g1: LineSegment StartX=0 StartY=-5 StartZ=0 EndX=-22.5 EndY=-5 EndZ=0
    g2: LineSegment StartX=-22.5 StartY=-5 StartZ=0 EndX=-22.5 EndY=-16.5 EndZ=0
    g3: LineSegment StartX=-22.5 StartY=-16.5 StartZ=0 EndX=0 EndY=-16.5 EndZ=0
  constraints (12):
    c: Coincident(g0,g1)
    c: Coincident(g1,g2)
    c: Coincident(g2,g3)
    c: Coincident(g3,g0)
    c: Vertical(g0)
    c: Vertical(g2)
    c: Horizontal(g1)
    c: Horizontal(g3)
    c: Coincident(g0,g-4)
    c: DistanceX(g1,g1) = 22.5
    c: DistanceY(g1,g-5) = 5
    c: DistanceY(g2,g2) = 11.5
FEATURE [PartDesign::Pocket] Pocket089
  BaseFeature = -> Pocket088
  Direction = (0,-1,2e-16)
  Length = 5
  Length2 = 5
  Profile = -> Sketch210
  ReferenceAxis = -> Sketch210 [N_Axis]
  Refine = true
  Suppressed = false
  Type = 0
FEATURE [Sketcher::SketchObject] Sketch211
  ArcFitTolerance = 1e-06
  AttachmentOffset = pos=(0,0,-5.3) rot=(0,0,1;0rad)
  AttachmentSupport = -> [Pocket089]
  ExternalGeometry = -> [Pocket089]
  FullyConstrained = true
  MakeInternals = false
  MapMode = 5
  Placement = pos=(0,0,-3.8) rot=(0,0,1;0rad)
  sketch-geometry (4):
    g0: LineSegment StartX=10 StartY=0 StartZ=0 EndX=11.05 EndY=-6.9208 EndZ=0
    g1: LineSegment StartX=16 StartY=0 StartZ=0 EndX=16.78 EndY=-5.14117 EndZ=0
    g2: LineSegment StartX=16 StartY=0 StartZ=0 EndX=10 EndY=0 EndZ=0
    g3: ArcOfCircle CenterX=13.915 CenterY=-6.03098 CenterZ=0 NormalX=0 NormalY=0 NormalZ=1 AngleXU=0 Radius=3 StartAngle=3.44273 EndAngle=6.58432
  constraints (14):
    c: PointOnObject(g0,g-4)
    c: PointOnObject(g1,g-3)
    c: Coincident(g2,g1)
    c: PointOnObject(g2,g0)
    c: Horizontal(g2)
    c: DistanceX(g-1,g0) = 10
    c: DistanceX(g2,g2) = 6
    c: Parallel(g1,g0)
    c: Coincident(g3,g0)
    c: Coincident(g3,g1)
    c: Diameter(g3) = 6
    c: Distance(g0) = 7
    c: Symmetric(g0,g1,g3)
    c: Distance(g1) = 5.2
FEATURE [PartDesign::Pad] Pad128
  BaseFeature = -> Pocket089
  Direction = (0,0,1)
  Length = 2.4
  Length2 = 10
  Profile = -> Sketch211
  ReferenceAxis = -> Sketch211 [N_Axis]
  Refine = true
  Reversed = true
  Suppressed = false
  Type = 0
FEATURE [Sketcher::SketchObject] Sketch212
  ArcFitTolerance = 1e-06
  AttachmentSupport = -> [Pad128]
  ExternalGeometry = -> [Pad128]
  FullyConstrained = true
  MakeInternals = false
  MapMode = 5
  Placement = pos=(0,0,-3.8) rot=(0,0,1;0rad)
  sketch-geometry (1):
    g0: Circle CenterX=13.915 CenterY=-6.03098 CenterZ=0 NormalX=0 NormalY=0 NormalZ=1 AngleXU=0 Radius=2.15
  constraints (2):
    c: Coincident(g0,g-3)
    c: Diameter(g0) = 4.3
FEATURE [PartDesign::Pad] Pad129
  BaseFeature = -> Pad128
  Direction = (0,0,1)
  Length = 2.3
  Length2 = 10
  Profile = -> Sketch212
  ReferenceAxis = -> Sketch212 [N_Axis]
  Refine = true
  Suppressed = false
  Type = 0
FEATURE [Sketcher::SketchObject] Sketch213
  ArcFitTolerance = 1e-06
  AttachmentSupport = -> [Pad129]
  ExternalGeometry = -> [Pad129]
  FullyConstrained = true
  MakeInternals = false
  MapMode = 5
  Placement = pos=(0,0,-1.5) rot=(0,0,1;0rad)
  sketch-geometry (1):
    g0: Circle CenterX=13.915 CenterY=-6.03098 CenterZ=0 NormalX=0 NormalY=0 NormalZ=1 AngleXU=0 Radius=1
  constraints (2):
    c: Coincident(g0,g-3)
    c: Diameter(g0) = 2
FEATURE [PartDesign::Pocket] Pocket090
  BaseFeature = -> Pad129
  Direction = (0,0,-1)
  Length = 5
  Length2 = 5
  Profile = -> Sketch213
  ReferenceAxis = -> Sketch213 [N_Axis]
  Refine = true
  Suppressed = false
  Type = 0
FEATURE [Sketcher::SketchObject] Sketch214
  ArcFitTolerance = 1e-06
  AttachmentOffset = pos=(0,0,-6) rot=(0,0,1;0rad)
  AttachmentSupport = -> [Pocket090]
  ExternalGeometry = -> [Pocket090]
  FullyConstrained = true
  MakeInternals = false
  MapMode = 5
  Placement = pos=(0,0,-4.5) rot=(0,0,1;0rad)
  sketch-geometry (4):
    g0: LineSegment StartX=21.3 StartY=0 StartZ=0 EndX=28.7 EndY=0 EndZ=0
    g1: LineSegment StartX=21.3 StartY=0 StartZ=0 EndX=23.055 EndY=-11.5676 EndZ=0
    g2: LineSegment StartX=28.7 StartY=0 StartZ=0 EndX=30.275 EndY=-10.3812 EndZ=0
    g3: ArcOfCircle CenterX=26.5753 CenterY=-10.4286 CenterZ=0 NormalX=0 NormalY=0 NormalZ=1 AngleXU=0 Radius=3.7 StartAngle=3.45453 EndAngle=6.29599
  constraints (13):
    c: PointOnObject(g0,g-1)
    c: Coincident(g1,g0)
    c: Coincident(g2,g0)
    c: Coincident(g3,g1)
    c: Coincident(g3,g2)
    c: Parallel(g1,g2)
    c: Distance(g0) = 7.4
    c: Distance(g1) = 11.7
    c: Diameter(g3) = 7.4
    c: PointOnObject(g0,g-1)
    c: Distance(g0,g-3) = 5.3
    c: Parallel(g-3,g1)
    c: Distance(g2) = 10.5
FEATURE [PartDesign::Pad] Pad130
  BaseFeature = -> Pocket090
  Direction = (0,0,1)
  Length = 2.5
  Length2 = 10
  Profile = -> Sketch214
  ReferenceAxis = -> Sketch214 [N_Axis]
  Refine = true
  Reversed = true
  Suppressed = false
  Type = 0
FEATURE [Sketcher::SketchObject] Sketch215
  ArcFitTolerance = 1e-06
  AttachmentSupport = -> [Pad130]
  ExternalGeometry = -> [Pad130]
  FullyConstrained = true
  MakeInternals = false
  MapMode = 5
  Placement = pos=(0,0,-4.5) rot=(0,0,1;0rad)
  sketch-geometry (1):
    g0: Circle CenterX=26.5753 CenterY=-10.4286 CenterZ=0 NormalX=0 NormalY=0 NormalZ=1 AngleXU=0 Radius=2.65
  constraints (2):
    c: Coincident(g0,g-3)
    c: Diameter(g0) = 5.3
FEATURE [PartDesign::Pad] Pad131
  BaseFeature = -> Pad130
  Direction = (0,0,1)
  Length = 2
  Length2 = 10
  Profile = -> Sketch215
  ReferenceAxis = -> Sketch215 [N_Axis]
  Refine = true
  Suppressed = false
  Type = 0
FEATURE [Sketcher::SketchObject] Sketch216
  ArcFitTolerance = 1e-06
  AttachmentSupport = -> [Pad131]
  ExternalGeometry = -> [Pad131]
  FullyConstrained = true
  MakeInternals = false
  MapMode = 5
  Placement = pos=(0,0,-2.5) rot=(0,0,1;0rad)
  sketch-geometry (1):
    g0: Circle CenterX=26.5753 CenterY=-10.4286 CenterZ=0 NormalX=0 NormalY=0 NormalZ=1 AngleXU=0 Radius=0.75
  constraints (2):
    c: Coincident(g0,g-3)
    c: Diameter(g0) = 1.5
FEATURE [PartDesign::Pocket] Pocket091
  BaseFeature = -> Pad131
  Direction = (0,0,-1)
  Length = 5
  Length2 = 5
  Profile = -> Sketch216
  ReferenceAxis = -> Sketch216 [N_Axis]
  Refine = true
  Suppressed = false
  Type = 0
FEATURE [Sketcher::SketchObject] Sketch217
  ArcFitTolerance = 1e-06
  AttachmentSupport = -> [Pocket091]
  ExternalGeometry = -> [Pocket091]
  FullyConstrained = true
  MakeInternals = false
  MapMode = 5
  Placement = pos=(0,0,0) rot=(0,0.707107,0.707107;3.14159rad)
  sketch-geometry (4):
    g0: LineSegment StartX=0 StartY=-5 StartZ=0 EndX=-22.5 EndY=-5 EndZ=0
    g1: LineSegment StartX=-22.5 StartY=-5 StartZ=0 EndX=-22.5 EndY=-6.2 EndZ=0
    g2: LineSegment StartX=-22.5 StartY=-6.2 StartZ=0 EndX=0 EndY=-6.2 EndZ=0
    g3: LineSegment StartX=0 StartY=-6.2 StartZ=0 EndX=0 EndY=-5 EndZ=0
  constraints (11):
    c: Coincident(g0,g1)
    c: Coincident(g1,g2)
    c: Coincident(g2,g3)
    c: Coincident(g3,g0)
    c: Horizontal(g0)
    c: Horizontal(g2)
    c: Vertical(g1)
    c: Vertical(g3)
    c: PointOnObject(g0,g-2)
    c: Coincident(g0,g-7)
    c: PointOnObject(g-3,g2)
FEATURE [PartDesign::Pad] Pad132
  BaseFeature = -> Pocket091
  Direction = (0,1,-2e-16)
  Length = 7.2
  Length2 = 10
  Profile = -> Sketch217
  ReferenceAxis = -> Sketch217 [N_Axis]
  Refine = true
  Suppressed = false
  Type = 0
FEATURE [Sketcher::SketchObject] Sketch218
  ArcFitTolerance = 1e-06
  AttachmentSupport = -> [Pad132]
  ExternalGeometry = -> [Pad132]
  FullyConstrained = true
  MakeInternals = false
  MapMode = 5
  Placement = pos=(0,0,-6.2) rot=(1,0,0;3.14159rad)
  sketch-geometry (3):
    g0: LineSegment StartX=22.5 StartY=-1.5 StartZ=0 EndX=22.5 EndY=-7.2 EndZ=0
    g1: LineSegment StartX=22.5 StartY=-7.2 StartZ=0 EndX=21.6349 EndY=-7.2 EndZ=0
    g2: LineSegment StartX=21.6349 StartY=-7.2 StartZ=0 EndX=22.5 EndY=-1.5 EndZ=0
  constraints (7):
    c: Coincident(g0,g-3)
    c: Coincident(g0,g-4)
    c: Coincident(g1,g0)
    c: PointOnObject(g1,g-4)
    c: Coincident(g2,g1)
    c: Coincident(g2,g0)
    c: Angle(g2,g0) = 0.150622
FEATURE [PartDesign::Pocket] Pocket092
  BaseFeature = -> Pad132
  Direction = (0,0,1)
  Length = 1.2
  Length2 = 5
  Profile = -> Sketch218
  ReferenceAxis = -> Sketch218 [N_Axis]
  Refine = true
  Suppressed = false
  Type = 0
FEATURE [Sketcher::SketchObject] Sketch219
  ArcFitTolerance = 1e-06
  AttachmentSupport = -> [Pocket092]
  ExternalGeometry = -> [Pocket092]
  FullyConstrained = true
  MakeInternals = false
  MapMode = 5
  Placement = pos=(0,1.5,0) rot=(0,0.707107,0.707107;3.14159rad)
  sketch-geometry (4):
    g0: LineSegment StartX=0 StartY=0 StartZ=0 EndX=-1.2 EndY=0 EndZ=0
    g1: LineSegment StartX=-1.2 StartY=0 StartZ=0 EndX=-1.2 EndY=-5 EndZ=0
    g2: LineSegment StartX=-1.2 StartY=-5 StartZ=0 EndX=0 EndY=-5 EndZ=0
    g3: LineSegment StartX=0 StartY=-5 StartZ=0 EndX=0 EndY=0 EndZ=0
  constraints (11):
    c: Coincident(g0,g1)
    c: Coincident(g1,g2)
    c: Coincident(g2,g3)
    c: Coincident(g3,g0)
    c: Horizontal(g0)
    c: Horizontal(g2)
    c: Vertical(g1)
    c: Vertical(g3)
    c: Coincident(g0,g-1)
    c: PointOnObject(g1,g-4)
    c: DistanceX(g2,g2) = 1.2
FEATURE [PartDesign::Pad] Pad133
  BaseFeature = -> Pocket092
  Direction = (0,1,-2e-16)
  Length = 5.7
  Length2 = 10
  Profile = -> Sketch219
  ReferenceAxis = -> Sketch219 [N_Axis]
  Refine = true
  Suppressed = false
  Type = 0
FEATURE [Sketcher::SketchObject] Sketch220
  ArcFitTolerance = 1e-06
  AttachmentSupport = -> [Pad133]
  ExternalGeometry = -> [Pad133]
  FullyConstrained = true
  MakeInternals = false
  MapMode = 5
  Placement = pos=(0,0,-6.2) rot=(1,0,0;3.14159rad)
  sketch-geometry (5):
    g0: LineSegment StartX=21.6349 StartY=-7.2 StartZ=0 EndX=22.5 EndY=-1.5 EndZ=0
    g1: LineSegment StartX=22.5 StartY=-1.5 StartZ=0 EndX=22.5 EndY=0 EndZ=0
    g2: LineSegment StartX=22.5 StartY=0 StartZ=0 EndX=21.3 EndY=1.4e-15 EndZ=0
    g3: LineSegment StartX=21.3 StartY=1.4e-15 StartZ=0 EndX=20.2072 EndY=-7.2 EndZ=0
    g4: LineSegment StartX=20.2072 StartY=-7.2 StartZ=0 EndX=21.6349 EndY=-7.2 EndZ=0
  constraints (11):
    c: Coincident(g0,g-4)
    c: Coincident(g0,g-5)
    c: Coincident(g1,g0)
    c: Coincident(g1,g-6)
    c: Coincident(g2,g1)
    c: Coincident(g2,g-6)
    c: Coincident(g3,g2)
    c: PointOnObject(g3,g-3)
    c: Coincident(g4,g3)
    c: Coincident(g4,g0)
    c: Parallel(g0,g3)
FEATURE [PartDesign::Pad] Pad134
  BaseFeature = -> Pad133
  Direction = (0,0,-1)
  Length = 10.3
  Length2 = 10
  Profile = -> Sketch220
  ReferenceAxis = -> Sketch220 [N_Axis]
  Refine = true
  Suppressed = false
  Type = 0
FEATURE [Sketcher::SketchObject] Sketch221
  ArcFitTolerance = 1e-06
  AttachmentSupport = -> [Pad134]
  ExternalGeometry = -> [Pad134]
  FullyConstrained = true
  MakeInternals = false
  MapMode = 5
  Placement = pos=(0,7.2,0) rot=(0,0.707107,0.707107;3.14159rad)
  sketch-geometry (4):
    g0: LineSegment StartX=0 StartY=-6.2 StartZ=0 EndX=-21.6349 EndY=-6.2 EndZ=0
    g1: LineSegment StartX=-21.6349 StartY=-6.2 StartZ=0 EndX=-21.6349 EndY=-16.5 EndZ=0
    g2: LineSegment StartX=-21.6349 StartY=-16.5 StartZ=0 EndX=0 EndY=-16.5 EndZ=0
    g3: LineSegment StartX=0 StartY=-16.5 StartZ=0 EndX=0 EndY=-6.2 EndZ=0
  constraints (10):
    c: Coincident(g0,g1)
    c: Coincident(g1,g2)
    c: Coincident(g2,g3)
    c: Coincident(g3,g0)
    c: Horizontal(g0)
    c: Horizontal(g2)
    c: Vertical(g1)
    c: Vertical(g3)
    c: Coincident(g0,g-3)
    c: Coincident(g1,g-5)
FEATURE [PartDesign::Pad] Pad135
  BaseFeature = -> Pad134
  Direction = (0,1,-2e-16)
  Length = 1.5
  Length2 = 10
  Profile = -> Sketch221
  ReferenceAxis = -> Sketch221 [N_Axis]
  Refine = true
  Reversed = true
  Suppressed = false
  Type = 0
FEATURE [Sketcher::SketchObject] Sketch222
  ArcFitTolerance = 1e-06
  AttachmentSupport = -> [Pad135]
  ExternalGeometry = -> [Pad135]
  FullyConstrained = true
  MakeInternals = false
  MapMode = 5
  Placement = pos=(0,0,-16.5) rot=(1,0,0;3.14159rad)
  sketch-geometry (4):
    g0: LineSegment StartX=21.3 StartY=0 StartZ=0 EndX=20.4349 EndY=-5.7 EndZ=0
    g1: LineSegment StartX=20.4349 StartY=-5.7 StartZ=0 EndX=0 EndY=-5.7 EndZ=0
    g2: LineSegment StartX=0 StartY=-5.7 StartZ=0 EndX=0 EndY=0 EndZ=0
    g3: LineSegment StartX=0 StartY=0 StartZ=0 EndX=21.3 EndY=0 EndZ=0
  constraints (8):
    c: Coincident(g0,g-3)
    c: Coincident(g0,g-4)
    c: Coincident(g1,g0)
    c: Coincident(g1,g-4)
    c: Coincident(g2,g1)
    c: Coincident(g2,g-1)
    c: Coincident(g3,g2)
    c: Coincident(g3,g0)
FEATURE [PartDesign::Pad] Pad136
  BaseFeature = -> Pad135
  Direction = (0,0,-1)
  Length = 1.2
  Length2 = 10
  Profile = -> Sketch222
  ReferenceAxis = -> Sketch222 [N_Axis]
  Refine = true
  Reversed = true
  Suppressed = false
  Type = 0
FEATURE [Sketcher::SketchObject] Sketch223
  ArcFitTolerance = 1e-06
  AttachmentSupport = -> [Pad136]
  ExternalGeometry = -> [Pad136]
  FullyConstrained = true
  MakeInternals = false
  MapMode = 5
  Placement = pos=(0,0,0) rot=(0.57735,-0.57735,-0.57735;2.0944rad)
  sketch-geometry (6):
    g0: LineSegment StartX=-5.7 StartY=-15.3 StartZ=0 EndX=-3.5 EndY=-15.3 EndZ=0
    g1: LineSegment StartX=-5.7 StartY=-15.3 StartZ=0 EndX=-5.7 EndY=-6.2 EndZ=0
    g2: LineSegment StartX=-5.7 StartY=-6.2 StartZ=0 EndX=9e-16 EndY=-6.2 EndZ=0
    g3: LineSegment StartX=9e-16 StartY=-6.2 StartZ=0 EndX=9e-16 EndY=-7.3 EndZ=0
    g4: LineSegment StartX=9e-16 StartY=-7.3 StartZ=0 EndX=-3.5 EndY=-7.3 EndZ=0
    g5: LineSegment StartX=-3.5 StartY=-7.3 StartZ=0 EndX=-3.5 EndY=-15.3 EndZ=0
  constraints (17):
    c: DistanceY(g-4,g-4) = 9.1
    c: Coincident(g0,g-5)
    c: PointOnObject(g0,g-5)
    c: Coincident(g1,g0)
    c: Coincident(g1,g-4)
    c: Coincident(g2,g1)
    c: Coincident(g3,g2)
    c: Vertical(g3)
    c: Coincident(g4,g3)
    c: Horizontal(g4)
    c: Coincident(g5,g4)
    c: Coincident(g5,g0)
    c: Vertical(g5)
    c: DistanceY(g3,g3) = 1.1
    c: Coincident(g2,g-3)
    c: DistanceX(g0,g0) = 2.2
    c: DistanceX(g-5,g-5) = 5.7
FEATURE [PartDesign::Pad] Pad137
  BaseFeature = -> Pad136
  Direction = (-1,0,0)
  Length = 1.5
  Length2 = 10
  Profile = -> Sketch223
  ReferenceAxis = -> Sketch223 [N_Axis]
  Refine = true
  Reversed = true
  Suppressed = false
  Type = 0
FEATURE [Sketcher::SketchObject] Sketch224
  ArcFitTolerance = 1e-06
  AttachmentSupport = -> [Pad137]
  ExternalGeometry = -> [Pad137]
  FullyConstrained = true
  MakeInternals = false
  MapMode = 5
  Placement = pos=(0,0,-16.5) rot=(1,0,0;3.14159rad)
  sketch-geometry (4):
    g0: ArcOfCircle CenterX=13.915 CenterY=6.03098 CenterZ=0 NormalX=0 NormalY=0 NormalZ=1 AngleXU=0 Radius=3 StartAngle=5.98205 EndAngle=9.12364
    g1: LineSegment StartX=11.05 StartY=6.9208 StartZ=0 EndX=8.90764 EndY=-7.2 EndZ=0
    g2: LineSegment StartX=16.78 StartY=5.14117 StartZ=0 EndX=14.9076 EndY=-7.2 EndZ=0
    g3: LineSegment StartX=14.9076 StartY=-7.2 StartZ=0 EndX=8.90764 EndY=-7.2 EndZ=0
  constraints (10):
    c: Tangent(g0,g-5) = -1.5708
    c: Coincident(g0,g-5)
    c: Coincident(g1,g0)
    c: PointOnObject(g1,g-6)
    c: Coincident(g2,g0)
    c: PointOnObject(g2,g-6)
    c: Coincident(g3,g2)
    c: Coincident(g3,g1)
    c: PointOnObject(g-4,g1)
    c: PointOnObject(g-3,g2)
FEATURE [PartDesign::Pad] Pad138
  BaseFeature = -> Pad137
  Direction = (0,0,-1)
  Length = 3.5
  Length2 = 10
  Profile = -> Sketch224
  ReferenceAxis = -> Sketch224 [N_Axis]
  Refine = true
  Reversed = true
  Suppressed = false
  Type = 0
FEATURE [PartDesign::Body] Body005  label="Pre_Left_Foot"
  AllowCompound = false
  Group = -> [Sketch203,Pad123,Sketch204,Pad124,Sketch205,Pad125,Sketch206,Pocket087,Sketch207,Pad126,Sketch208,Pad127,Sketch209,Pocket088,Sketch210,Pocket089,Sketch211,Pad128,Sketch212,Pad129,Sketch213,Pocket090,Sketch214,Pad130,Sketch215,Pad131,Sketch216,Pocket091,Sketch217,Pad132,Sketch218,Pocket092,Sketch219,Pad133,Sketch220,Pad134,Sketch221,Pad135,Sketch222,Pad136,Sketch223,Pad137,Sketch224,Pad138,+35 more]
  Origin = -> Origin005
  Placement = pos=(-29.0207,-16.7,-43.6738) rot=(-0.631029,0.548545,-0.548545;4.26744rad)
  Tip = -> Pocket186
COMPONENT P6 — recipe-attached ("Arm_Rod_Collar1", modeled in this document).
Construction recipe (the document's own serialized feature program — sketch geometry with constraints, then the solid features built on it; lengths are millimeters unless a unit is written):

FEATURE [Sketcher::SketchObject] Sketch296
  ArcFitTolerance = 1e-06
  AttachmentSupport = -> [XY_Plane011]
  FullyConstrained = true
  MakeInternals = false
  MapMode = 5
  sketch-geometry (2):
    g0: Circle CenterX=0 CenterY=0 CenterZ=0 NormalX=0 NormalY=0 NormalZ=1 AngleXU=0 Radius=0.8
    g1: Circle CenterX=0 CenterY=0 CenterZ=0 NormalX=0 NormalY=0 NormalZ=1 AngleXU=0 Radius=1.425
  constraints (4):
    c: Coincident(g0,g-1)
    c: Coincident(g1,g0)
    c: Diameter(g0) = 1.6
    c: Diameter(g1) = 2.85
FEATURE [PartDesign::Pad] Pad176
  Direction = (0,0,1)
  Length = 3.3
  Length2 = 10
  Profile = -> Sketch296
  ReferenceAxis = -> Sketch296 [N_Axis]
  Refine = true
  Suppressed = false
  Type = 0
FEATURE [PartDesign::Body] Body011  label="Arm_Rod_Collar1"
  AllowCompound = false
  Group = -> [Sketch296,Pad176]
  Origin = -> Origin011
  Placement = pos=(-15.5,-11,7.6) rot=(1,0,0;1.5708rad)
  Tip = -> Pad176
